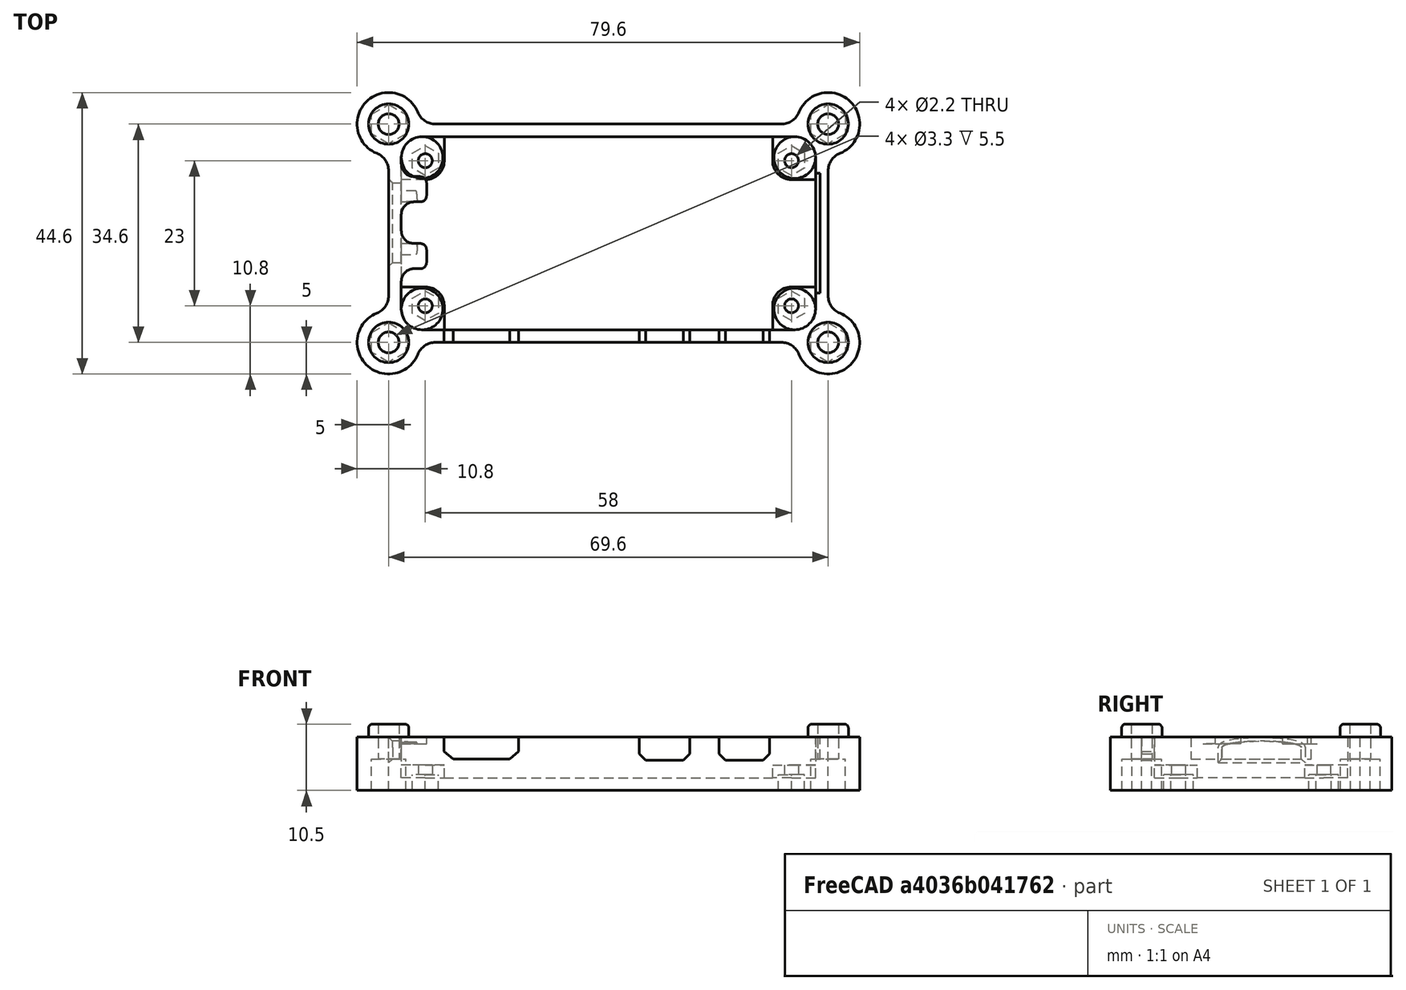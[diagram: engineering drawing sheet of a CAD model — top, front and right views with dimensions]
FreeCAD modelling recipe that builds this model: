
FCSTD DOCUMENT  (FreeCAD 0.18R13830 (Git))
Label: MMDVM_HS_Bottom-SLIM
License: CreativeCommons Attribution-NonCommercial-ShareAlike
LicenseURL: http://creativecommons.org/licenses/by-nc-sa/4.0/
objects: Sketcher::SketchObject×14, PartDesign::Pocket×7, PartDesign::Fillet×5, PartDesign::Pad×4, PartDesign::Hole×2, PartDesign::Chamfer×1, PartDesign::Body×1, Mesh::Feature×1
note: 47 computed .brp shape members not serialized (recipe doc carries the construction recipe); baked Part::Feature solids carry a one-line shape summary decoded from their .brp

FEATURE [Sketcher::SketchObject] Sketch
  MapMode = 5
  Support = -> [XY_Plane]
  sketch-geometry (24):
    g0: LineSegment [constr] StartX=-32.5 StartY=15 StartZ=0 EndX=32.5 EndY=15 EndZ=0
    g1: LineSegment [constr] StartX=32.5 StartY=15 StartZ=0 EndX=32.5 EndY=-15 EndZ=0
    g2: LineSegment [constr] StartX=32.5 StartY=-15 StartZ=0 EndX=-32.5 EndY=-15 EndZ=0
    g3: LineSegment [constr] StartX=-32.5 StartY=-15 StartZ=0 EndX=-32.5 EndY=15 EndZ=0
    g4: LineSegment [constr] StartX=-29 StartY=11.5 StartZ=0 EndX=29 EndY=11.5 EndZ=0
    g5: LineSegment [constr] StartX=29 StartY=11.5 StartZ=0 EndX=29 EndY=-11.5 EndZ=0
    g6: LineSegment [constr] StartX=29 StartY=-11.5 StartZ=0 EndX=-29 EndY=-11.5 EndZ=0
    g7: LineSegment [constr] StartX=-29 StartY=-11.5 StartZ=0 EndX=-29 EndY=11.5 EndZ=0
    g8: Circle CenterX=-29 CenterY=11.5 CenterZ=0 NormalX=0 NormalY=0 NormalZ=1 AngleXU=0 Radius=1.375
    g9: Circle CenterX=29 CenterY=11.5 CenterZ=0 NormalX=0 NormalY=0 NormalZ=1 AngleXU=0 Radius=1.375
    g10: Circle CenterX=29 CenterY=-11.5 CenterZ=0 NormalX=0 NormalY=0 NormalZ=1 AngleXU=0 Radius=1.375
    g11: Circle CenterX=-29 CenterY=-11.5 CenterZ=0 NormalX=0 NormalY=0 NormalZ=1 AngleXU=0 Radius=1.375
    g12: LineSegment [constr] StartX=-29.5 StartY=12 StartZ=0 EndX=29.5 EndY=12 EndZ=0
    g13: LineSegment [constr] StartX=29.5 StartY=12 StartZ=0 EndX=29.5 EndY=-12 EndZ=0
    g14: LineSegment [constr] StartX=29.5 StartY=-12 StartZ=0 EndX=-29.5 EndY=-12 EndZ=0
    g15: LineSegment [constr] StartX=-29.5 StartY=-12 StartZ=0 EndX=-29.5 EndY=12 EndZ=0
    g16: ArcOfCircle CenterX=-29.5 CenterY=12 CenterZ=0 NormalX=0 NormalY=0 NormalZ=1 AngleXU=0 Radius=3 StartAngle=1.5708 EndAngle=3.1416
    g17: ArcOfCircle CenterX=29.5 CenterY=12 CenterZ=0 NormalX=0 NormalY=0 NormalZ=1 AngleXU=0 Radius=3 StartAngle=1.42077e-07 EndAngle=1.5708
    g18: ArcOfCircle CenterX=29.5 CenterY=-12 CenterZ=0 NormalX=0 NormalY=0 NormalZ=1 AngleXU=0 Radius=3 StartAngle=4.71239 EndAngle=6.28319
    g19: ArcOfCircle CenterX=-29.5 CenterY=-12 CenterZ=0 NormalX=0 NormalY=0 NormalZ=1 AngleXU=0 Radius=3 StartAngle=3.14159 EndAngle=4.71239
    g20: LineSegment StartX=-29.5 StartY=15 StartZ=0 EndX=29.5 EndY=15 EndZ=0
    g21: LineSegment StartX=32.5 StartY=12 StartZ=0 EndX=32.5 EndY=-12 EndZ=0
    g22: LineSegment StartX=29.5 StartY=-15 StartZ=0 EndX=-29.5 EndY=-15 EndZ=0
    g23: LineSegment StartX=-32.5 StartY=-12 StartZ=0 EndX=-32.5 EndY=12 EndZ=0
  constraints (68):
    c: Coincident(g0,g1)
    c: Coincident(g1,g2)
    c: Coincident(g2,g3)
    c: Coincident(g3,g0)
    c: Horizontal(g0)
    c: Horizontal(g2)
    c: Vertical(g1)
    c: Vertical(g3)
    c: DistanceX(g0,g0) = 65
    c: DistanceY(g1,g1) = 30
    c: Symmetric(g0,g0,g-2)
    c: Symmetric(g0,g1,g-1)
    c: Coincident(g4,g5)
    c: Coincident(g5,g6)
    c: Coincident(g6,g7)
    c: Coincident(g7,g4)
    c: Horizontal(g4)
    c: Horizontal(g6)
    c: Vertical(g5)
    c: Vertical(g7)
    c: DistanceX(g4,g4) = 58
    c: DistanceY(g5,g5) = 23
    c: Symmetric(g4,g5,g-1)
    c: Symmetric(g4,g4,g-2)
    c: Coincident(g8,g4)
    c: Coincident(g9,g4)
    c: Coincident(g10,g5)
    c: Coincident(g11,g6)
    c: Radius(g11) = 1.375
    c: Radius(g8) = 1.375
    c: Radius(g9) = 1.375
    c: Radius(g10) = 1.375
    c: Coincident(g12,g13)
    c: Coincident(g13,g14)
    c: Coincident(g14,g15)
    c: Coincident(g15,g12)
    c: Horizontal(g12)
    c: Horizontal(g14)
    c: Vertical(g13)
    c: Vertical(g15)
    c: DistanceX(g4,g12) = 0.5
    c: DistanceY(g4,g12) = 0.5
    c: DistanceY(g13,g5) = 0.5
    c: DistanceX(g14,g6) = 0.5
    c: Coincident(g16,g12)
    c: Radius(g16) = 3
    c: Coincident(g17,g12)
    c: Radius(g17) = 3
    c: Coincident(g18,g13)
    c: Radius(g18) = 3
    c: Coincident(g19,g14)
    c: Radius(g19) = 3
    c: PointOnObject(g16,g0)
    c: PointOnObject(g17,g1)
    c: PointOnObject(g18,g2)
    c: PointOnObject(g19,g3)
    c: Coincident(g20,g16)
    c: Horizontal(g20)
    c: Coincident(g20,g17)
    c: Coincident(g21,g17)
    c: Vertical(g21)
    c: Coincident(g18,g21)
    c: Coincident(g22,g18)
    c: Horizontal(g22)
    c: Coincident(g19,g22)
    c: Coincident(g23,g19)
    c: Vertical(g23)
    c: Coincident(g23,g16)
FEATURE [Sketcher::SketchObject] Sketch001
  MapMode = 5
  Support = -> [XY_Plane]
  expr: Constraints[8] = Sketch.Constraints[8]
  expr: Constraints[41] = Sketch.Constraints[41]
  expr: Constraints[9] = Sketch.Constraints[9]
  expr: Constraints[45] = Sketch.Constraints[45]
  expr: Constraints[43] = Sketch.Constraints[43]
  expr: Constraints[42] = Sketch.Constraints[42]
  expr: Constraints[20] = Sketch.Constraints[20]
  expr: Constraints[21] = Sketch.Constraints[21]
  expr: Constraints[28] = Sketch.Constraints[28]
  expr: Constraints[29] = Sketch.Constraints[29]
  expr: Constraints[30] = Sketch.Constraints[30]
  expr: Constraints[40] = Sketch.Constraints[40]
  expr: Constraints[31] = Sketch.Constraints[31]
  expr: Constraints[47] = Sketch.Constraints[47]
  expr: Constraints[49] = Sketch.Constraints[49]
  expr: Constraints[51] = Sketch.Constraints[51]
  sketch-geometry (64):
    g0: LineSegment [constr] StartX=-32.5 StartY=15 StartZ=0 EndX=32.5 EndY=15 EndZ=0
    g1: LineSegment [constr] StartX=32.5 StartY=15 StartZ=0 EndX=32.5 EndY=-15 EndZ=0
    g2: LineSegment [constr] StartX=32.5 StartY=-15 StartZ=0 EndX=-32.5 EndY=-15 EndZ=0
    g3: LineSegment [constr] StartX=-32.5 StartY=-15 StartZ=0 EndX=-32.5 EndY=15 EndZ=0
    g4: LineSegment [constr] StartX=-29 StartY=11.5 StartZ=0 EndX=29 EndY=11.5 EndZ=0
    g5: LineSegment [constr] StartX=29 StartY=11.5 StartZ=0 EndX=29 EndY=-11.5 EndZ=0
    g6: LineSegment [constr] StartX=29 StartY=-11.5 StartZ=0 EndX=-29 EndY=-11.5 EndZ=0
    g7: LineSegment [constr] StartX=-29 StartY=-11.5 StartZ=0 EndX=-29 EndY=11.5 EndZ=0
    g8: Circle [constr] CenterX=-29 CenterY=11.5 CenterZ=0 NormalX=0 NormalY=0 NormalZ=1 AngleXU=0 Radius=1.375
    g9: Circle [constr] CenterX=29 CenterY=11.5 CenterZ=0 NormalX=0 NormalY=0 NormalZ=1 AngleXU=0 Radius=1.375
    g10: Circle [constr] CenterX=29 CenterY=-11.5 CenterZ=0 NormalX=0 NormalY=0 NormalZ=1 AngleXU=0 Radius=1.375
    g11: Circle [constr] CenterX=-29 CenterY=-11.5 CenterZ=0 NormalX=0 NormalY=0 NormalZ=1 AngleXU=0 Radius=1.375
    g12: LineSegment [constr] StartX=-29.5 StartY=12 StartZ=0 EndX=29.5 EndY=12 EndZ=0
    g13: LineSegment [constr] StartX=29.5 StartY=12 StartZ=0 EndX=29.5 EndY=-12 EndZ=0
    g14: LineSegment [constr] StartX=29.5 StartY=-12 StartZ=0 EndX=-29.5 EndY=-12 EndZ=0
    g15: LineSegment [constr] StartX=-29.5 StartY=-12 StartZ=0 EndX=-29.5 EndY=12 EndZ=0
    g16: ArcOfCircle [constr] CenterX=-29.5 CenterY=12 CenterZ=0 NormalX=0 NormalY=0 NormalZ=1 AngleXU=0 Radius=3 StartAngle=1.5708 EndAngle=3.14159
    g17: ArcOfCircle [constr] CenterX=29.5 CenterY=12 CenterZ=0 NormalX=0 NormalY=0 NormalZ=1 AngleXU=0 Radius=3 StartAngle=2.8425e-08 EndAngle=1.5708
    g18: ArcOfCircle [constr] CenterX=29.5 CenterY=-12 CenterZ=0 NormalX=0 NormalY=0 NormalZ=1 AngleXU=0 Radius=3 StartAngle=4.71239 EndAngle=6.28319
    g19: ArcOfCircle [constr] CenterX=-29.5 CenterY=-12 CenterZ=0 NormalX=0 NormalY=0 NormalZ=1 AngleXU=0 Radius=3 StartAngle=3.14159 EndAngle=4.71239
    g20: LineSegment [constr] StartX=-29.5 StartY=15 StartZ=0 EndX=29.5 EndY=15 EndZ=0
    g21: LineSegment [constr] StartX=32.5 StartY=12 StartZ=0 EndX=32.5 EndY=-12 EndZ=0
    g22: LineSegment [constr] StartX=29.5 StartY=-15 StartZ=0 EndX=-29.5 EndY=-15 EndZ=0
    g23: LineSegment [constr] StartX=-32.5 StartY=-12 StartZ=0 EndX=-32.5 EndY=12 EndZ=0
    g24: ArcOfCircle [constr] CenterX=-29.5 CenterY=12 CenterZ=0 NormalX=0 NormalY=0 NormalZ=1 AngleXU=0 Radius=3.3 StartAngle=1.5708 EndAngle=3.14159
    g25: ArcOfCircle [constr] CenterX=29.5 CenterY=12 CenterZ=0 NormalX=0 NormalY=0 NormalZ=1 AngleXU=0 Radius=3.3 StartAngle=-2.2e-10 EndAngle=1.5708
    g26: ArcOfCircle [constr] CenterX=29.5 CenterY=-12 CenterZ=0 NormalX=0 NormalY=0 NormalZ=1 AngleXU=0 Radius=3.3 StartAngle=4.71239 EndAngle=6.28319
    g27: ArcOfCircle [constr] CenterX=-29.5 CenterY=-12 CenterZ=0 NormalX=0 NormalY=0 NormalZ=1 AngleXU=0 Radius=3.3 StartAngle=3.14159 EndAngle=4.71239
    g28: LineSegment [constr] StartX=-32.8 StartY=12 StartZ=0 EndX=-32.8 EndY=-12 EndZ=0
    g29: LineSegment [constr] StartX=-29.5 StartY=15.3 StartZ=0 EndX=29.5 EndY=15.3 EndZ=0
    g30: LineSegment [constr] StartX=32.8 StartY=12 StartZ=0 EndX=32.8 EndY=-12 EndZ=0
    g31: LineSegment [constr] StartX=29.5 StartY=-15.3 StartZ=0 EndX=-29.5 EndY=-15.3 EndZ=0
    g32: LineSegment [constr] StartX=-34.8 StartY=17.3 StartZ=0 EndX=34.8 EndY=17.3 EndZ=0
    g33: LineSegment [constr] StartX=34.8 StartY=17.3 StartZ=0 EndX=34.8 EndY=-17.3 EndZ=0
    g34: LineSegment [constr] StartX=34.8 StartY=-17.3 StartZ=0 EndX=-34.8 EndY=-17.3 EndZ=0
    g35: LineSegment [constr] StartX=-34.8 StartY=-17.3 StartZ=0 EndX=-34.8 EndY=17.3 EndZ=0
    g36: Circle [constr] CenterX=34.8 CenterY=17.3 CenterZ=0 NormalX=0 NormalY=0 NormalZ=1 AngleXU=0 Radius=5
    g37: Circle [constr] CenterX=34.8 CenterY=-17.3 CenterZ=0 NormalX=0 NormalY=0 NormalZ=1 AngleXU=0 Radius=5
    g38: Circle [constr] CenterX=-34.8 CenterY=-17.3 CenterZ=0 NormalX=0 NormalY=0 NormalZ=1 AngleXU=0 Radius=5
    g39: Circle [constr] CenterX=-34.8 CenterY=17.3 CenterZ=0 NormalX=0 NormalY=0 NormalZ=1 AngleXU=0 Radius=5
    g40: Circle [constr] CenterX=27.3838 CenterY=20.3 CenterZ=0 NormalX=0 NormalY=0 NormalZ=1 AngleXU=0 Radius=3
    g41: Circle [constr] CenterX=-27.3838 CenterY=20.3 CenterZ=0 NormalX=0 NormalY=0 NormalZ=1 AngleXU=0 Radius=3
    g42: Circle [constr] CenterX=-37.8 CenterY=9.8838 CenterZ=0 NormalX=0 NormalY=0 NormalZ=1 AngleXU=0 Radius=3
    g43: Circle [constr] CenterX=-37.8 CenterY=-9.8838 CenterZ=0 NormalX=0 NormalY=0 NormalZ=1 AngleXU=0 Radius=3
    g44: Circle [constr] CenterX=-27.3838 CenterY=-20.3 CenterZ=0 NormalX=0 NormalY=0 NormalZ=1 AngleXU=0 Radius=3
    g45: Circle [constr] CenterX=27.3838 CenterY=-20.3 CenterZ=0 NormalX=0 NormalY=0 NormalZ=1 AngleXU=0 Radius=3
    g46: Circle [constr] CenterX=37.8 CenterY=-9.8838 CenterZ=0 NormalX=0 NormalY=0 NormalZ=1 AngleXU=0 Radius=3
    g47: Circle [constr] CenterX=37.8 CenterY=9.8838 CenterZ=0 NormalX=0 NormalY=0 NormalZ=1 AngleXU=0 Radius=3
    g48: ArcOfCircle CenterX=34.8 CenterY=17.3 CenterZ=0 NormalX=0 NormalY=0 NormalZ=1 AngleXU=0 Radius=5 StartAngle=5.09679 EndAngle=9.04038
    g49: ArcOfCircle CenterX=27.3838 CenterY=20.3 CenterZ=0 NormalX=0 NormalY=0 NormalZ=1 AngleXU=0 Radius=3 StartAngle=4.71239 EndAngle=5.89879
    g50: ArcOfCircle CenterX=37.8 CenterY=9.8838 CenterZ=0 NormalX=0 NormalY=0 NormalZ=1 AngleXU=0 Radius=3 StartAngle=1.95519 EndAngle=3.14159
    g51: ArcOfCircle CenterX=37.8 CenterY=-9.8838 CenterZ=0 NormalX=0 NormalY=0 NormalZ=1 AngleXU=0 Radius=3 StartAngle=3.14159 EndAngle=4.32799
    g52: ArcOfCircle CenterX=34.8 CenterY=-17.3 CenterZ=0 NormalX=0 NormalY=0 NormalZ=1 AngleXU=0 Radius=5 StartAngle=3.52599 EndAngle=7.46958
    g53: ArcOfCircle CenterX=27.3838 CenterY=-20.3 CenterZ=0 NormalX=0 NormalY=0 NormalZ=1 AngleXU=0 Radius=3 StartAngle=0.384397 EndAngle=1.5708
    g54: ArcOfCircle CenterX=-27.3838 CenterY=-20.3 CenterZ=0 NormalX=0 NormalY=0 NormalZ=1 AngleXU=0 Radius=3 StartAngle=1.5708 EndAngle=2.7572
    g55: ArcOfCircle CenterX=-34.8 CenterY=-17.3 CenterZ=0 NormalX=0 NormalY=0 NormalZ=1 AngleXU=0 Radius=5 StartAngle=1.95519 EndAngle=5.89879
    g56: ArcOfCircle CenterX=-37.8 CenterY=-9.8838 CenterZ=0 NormalX=0 NormalY=0 NormalZ=1 AngleXU=0 Radius=3 StartAngle=5.09679 EndAngle=6.28319
    g57: ArcOfCircle CenterX=-37.8 CenterY=9.8838 CenterZ=0 NormalX=0 NormalY=0 NormalZ=1 AngleXU=0 Radius=3 StartAngle=6.28319 EndAngle=7.46958
    g58: ArcOfCircle CenterX=-34.8 CenterY=17.3 CenterZ=0 NormalX=0 NormalY=0 NormalZ=1 AngleXU=0 Radius=5 StartAngle=0.384397 EndAngle=4.32799
    g59: ArcOfCircle CenterX=-27.3838 CenterY=20.3 CenterZ=0 NormalX=0 NormalY=0 NormalZ=1 AngleXU=0 Radius=3 StartAngle=3.52599 EndAngle=4.71239
    g60: LineSegment StartX=-27.3838 StartY=17.3 StartZ=0 EndX=27.3838 EndY=17.3 EndZ=0
    g61: LineSegment StartX=34.8 StartY=9.8838 StartZ=0 EndX=34.8 EndY=-9.8838 EndZ=0
    g62: LineSegment StartX=27.3838 StartY=-17.3 StartZ=0 EndX=-27.3838 EndY=-17.3 EndZ=0
    g63: LineSegment StartX=-34.8 StartY=-9.8838 StartZ=0 EndX=-34.8 EndY=9.8838 EndZ=0
  constraints (184):
    c: Coincident(g0,g1)
    c: Coincident(g1,g2)
    c: Coincident(g2,g3)
    c: Coincident(g3,g0)
    c: Horizontal(g0)
    c: Horizontal(g2)
    c: Vertical(g1)
    c: Vertical(g3)
    c: DistanceX(g0,g0) = 65
    c: DistanceY(g1,g1) = 30
    c: Symmetric(g0,g0,g-2)
    c: Symmetric(g0,g1,g-1)
    c: Coincident(g4,g5)
    c: Coincident(g5,g6)
    c: Coincident(g6,g7)
    c: Coincident(g7,g4)
    c: Horizontal(g4)
    c: Horizontal(g6)
    c: Vertical(g5)
    c: Vertical(g7)
    c: DistanceX(g4,g4) = 58
    c: DistanceY(g5,g5) = 23
    c: Symmetric(g4,g5,g-1)
    c: Symmetric(g4,g4,g-2)
    c: Coincident(g8,g4)
    c: Coincident(g9,g4)
    c: Coincident(g10,g5)
    c: Coincident(g11,g6)
    c: Radius(g11) = 1.375
    c: Radius(g8) = 1.375
    c: Radius(g9) = 1.375
    c: Radius(g10) = 1.375
    c: Coincident(g12,g13)
    c: Coincident(g13,g14)
    c: Coincident(g14,g15)
    c: Coincident(g15,g12)
    c: Horizontal(g12)
    c: Horizontal(g14)
    c: Vertical(g13)
    c: Vertical(g15)
    c: DistanceX(g4,g12) = 0.5
    c: DistanceY(g4,g12) = 0.5
    c: DistanceY(g13,g5) = 0.5
    c: DistanceX(g14,g6) = 0.5
    c: Coincident(g16,g12)
    c: Radius(g16) = 3
    c: Coincident(g17,g12)
    c: Radius(g17) = 3
    c: Coincident(g18,g13)
    c: Radius(g18) = 3
    c: Coincident(g19,g14)
    c: Radius(g19) = 3
    c: PointOnObject(g16,g0)
    c: PointOnObject(g17,g1)
    c: PointOnObject(g18,g2)
    c: PointOnObject(g19,g3)
    c: Coincident(g20,g16)
    c: Horizontal(g20)
    c: Coincident(g20,g17)
    c: Coincident(g21,g17)
    c: Vertical(g21)
    c: Coincident(g18,g21)
    c: Coincident(g22,g18)
    c: Horizontal(g22)
    c: Coincident(g19,g22)
    c: Coincident(g23,g19)
    c: Vertical(g23)
    c: Coincident(g23,g16)
    c: Coincident(g24,g12)
    c: Radius(g24) = 3.3
    c: Coincident(g25,g12)
    c: Radius(g25) = 3.3
    c: Coincident(g26,g13)
    c: Radius(g26) = 3.3
    c: Coincident(g27,g14)
    c: Radius(g27) = 3.3
    c: Vertical(g28)
    c: DistanceX(g28,g2) = 0.3
    c: Coincident(g27,g28)
    c: Coincident(g28,g24)
    c: Horizontal(g29)
    c: DistanceY(g0,g29) = 0.3
    c: Coincident(g24,g29)
    c: Coincident(g25,g29)
    c: Vertical(g30)
    c: DistanceX(g0,g30) = 0.3
    c: Coincident(g25,g30)
    c: Coincident(g30,g26)
    c: Horizontal(g31)
    c: DistanceY(g31,g1) = 0.3
    c: Coincident(g31,g26)
    c: Coincident(g31,g27)
    c: Coincident(g32,g33)
    c: Coincident(g33,g34)
    c: Coincident(g34,g35)
    c: Coincident(g35,g32)
    c: Horizontal(g32)
    c: Horizontal(g34)
    c: Vertical(g33)
    c: Vertical(g35)
    c: DistanceY(g25,g32) = 2
    c: DistanceX(g25,g32) = 2
    c: DistanceY(g33,g26) = 2
    c: DistanceX(g34,g27) = 2
    c: Coincident(g36,g32)
    c: Coincident(g37,g33)
    c: Coincident(g38,g34)
    c: Coincident(g39,g32)
    c: Radius(g39) = 5
    c: Radius(g38) = 5
    c: Radius(g37) = 5
    c: Radius(g36) = 5
    c: Radius(g40) = 3
    c: Tangent(g40,g36)
    c: Tangent(g40,g32)
    c: Tangent(g47,g36)
    c: Radius(g47) = 3
    c: Tangent(g47,g33)
    c: Radius(g46) = 3
    c: Tangent(g46,g37)
    c: Tangent(g46,g33)
    c: Radius(g45) = 3
    c: Tangent(g45,g37)
    c: Tangent(g45,g34)
    c: Radius(g44) = 3
    c: Tangent(g44,g34)
    c: Tangent(g44,g38)
    c: Radius(g43) = 3
    c: Tangent(g43,g38)
    c: Tangent(g43,g35)
    c: Radius(g42) = 3
    c: Tangent(g42,g35)
    c: Tangent(g42,g39)
    c: Radius(g41) = 3
    c: Tangent(g41,g32)
    c: Tangent(g41,g39)
    c: Coincident(g48,g32)
    c: PointOnObject(g48,g36)
    c: Coincident(g49,g40)
    c: PointOnObject(g49,g40)
    c: Coincident(g50,g47)
    c: PointOnObject(g50,g47)
    c: Coincident(g51,g46)
    c: PointOnObject(g51,g46)
    c: Coincident(g52,g33)
    c: PointOnObject(g52,g37)
    c: Coincident(g53,g45)
    c: PointOnObject(g53,g45)
    c: Coincident(g54,g44)
    c: PointOnObject(g54,g44)
    c: Coincident(g55,g34)
    c: PointOnObject(g55,g38)
    c: Coincident(g56,g43)
    c: PointOnObject(g56,g43)
    c: Coincident(g57,g42)
    c: PointOnObject(g57,g42)
    c: Coincident(g58,g32)
    c: PointOnObject(g58,g39)
    c: Coincident(g59,g41)
    c: PointOnObject(g59,g41)
    c: Coincident(g49,g48)
    c: Coincident(g48,g50)
    c: Coincident(g51,g52)
    c: Coincident(g52,g53)
    c: Coincident(g54,g55)
    c: Coincident(g55,g56)
    c: Coincident(g57,g58)
    c: Coincident(g58,g59)
    c: PointOnObject(g60,g32)
    c: Horizontal(g60)
    c: PointOnObject(g61,g33)
    c: Vertical(g61)
    c: PointOnObject(g62,g34)
    c: Horizontal(g62)
    c: PointOnObject(g63,g35)
    c: Vertical(g63)
    c: Coincident(g59,g60)
    c: Coincident(g60,g49)
    c: Coincident(g50,g61)
    c: Coincident(g61,g51)
    c: Coincident(g53,g62)
    c: Coincident(g54,g62)
    c: Coincident(g56,g63)
    c: Coincident(g57,g63)
FEATURE [PartDesign::Pad] Pad
  Length = 8.5
  Length2 = 100
  Profile = -> Sketch001
  Type = 0
FEATURE [Sketcher::SketchObject] Sketch002
  MapMode = 5
  Placement = pos=(0,0,8.5) rot=(0,0,1;0rad)
  Support = -> [Pad]
  expr: Constraints[133] = Sketch001.Constraints[133]
  expr: Constraints[130] = Sketch001.Constraints[130]
  expr: Constraints[112] = Sketch001.Constraints[112]
  expr: Constraints[127] = Sketch001.Constraints[127]
  expr: Constraints[124] = Sketch001.Constraints[124]
  expr: Constraints[110] = Sketch001.Constraints[110]
  expr: Constraints[51] = Sketch001.Constraints[51]
  expr: Constraints[100] = Sketch001.Constraints[100]
  expr: Constraints[77] = Sketch001.Constraints[77]
  expr: Constraints[89] = Sketch001.Constraints[89]
  expr: Constraints[118] = Sketch001.Constraints[118]
  expr: Constraints[85] = Sketch001.Constraints[85]
  expr: Constraints[103] = Sketch001.Constraints[103]
  expr: Constraints[111] = Sketch001.Constraints[111]
  expr: Constraints[71] = Sketch001.Constraints[71]
  expr: Constraints[49] = Sketch001.Constraints[49]
  expr: Constraints[102] = Sketch001.Constraints[102]
  expr: Constraints[69] = Sketch001.Constraints[69]
  expr: Constraints[47] = Sketch001.Constraints[47]
  expr: Constraints[73] = Sketch001.Constraints[73]
  expr: Constraints[75] = Sketch001.Constraints[75]
  expr: Constraints[31] = Sketch001.Constraints[31]
  expr: Constraints[116] = Sketch001.Constraints[116]
  expr: Constraints[40] = Sketch001.Constraints[40]
  expr: Constraints[30] = Sketch001.Constraints[30]
  expr: Constraints[29] = Sketch001.Constraints[29]
  expr: Constraints[121] = Sketch001.Constraints[121]
  expr: Constraints[28] = Sketch001.Constraints[28]
  expr: Constraints[21] = Sketch001.Constraints[21]
  expr: Constraints[20] = Sketch001.Constraints[20]
  expr: Constraints[45] = Sketch001.Constraints[45]
  expr: Constraints[108] = Sketch001.Constraints[108]
  expr: Constraints[43] = Sketch001.Constraints[43]
  expr: Constraints[42] = Sketch001.Constraints[42]
  expr: Constraints[101] = Sketch001.Constraints[101]
  expr: Constraints[109] = Sketch001.Constraints[109]
  expr: Constraints[41] = Sketch001.Constraints[41]
  expr: Constraints[9] = Sketch001.Constraints[9]
  expr: Constraints[81] = Sketch001.Constraints[81]
  expr: Constraints[8] = Sketch001.Constraints[8]
  sketch-geometry (64):
    g0: LineSegment [constr] StartX=-32.5 StartY=15 StartZ=0 EndX=32.5 EndY=15 EndZ=0
    g1: LineSegment [constr] StartX=32.5 StartY=15 StartZ=0 EndX=32.5 EndY=-15 EndZ=0
    g2: LineSegment [constr] StartX=32.5 StartY=-15 StartZ=0 EndX=-32.5 EndY=-15 EndZ=0
    g3: LineSegment [constr] StartX=-32.5 StartY=-15 StartZ=0 EndX=-32.5 EndY=15 EndZ=0
    g4: LineSegment [constr] StartX=-29 StartY=11.5 StartZ=0 EndX=29 EndY=11.5 EndZ=0
    g5: LineSegment [constr] StartX=29 StartY=11.5 StartZ=0 EndX=29 EndY=-11.5 EndZ=0
    g6: LineSegment [constr] StartX=29 StartY=-11.5 StartZ=0 EndX=-29 EndY=-11.5 EndZ=0
    g7: LineSegment [constr] StartX=-29 StartY=-11.5 StartZ=0 EndX=-29 EndY=11.5 EndZ=0
    g8: Circle [constr] CenterX=-29 CenterY=11.5 CenterZ=0 NormalX=0 NormalY=0 NormalZ=1 AngleXU=0 Radius=1.375
    g9: Circle [constr] CenterX=29 CenterY=11.5 CenterZ=0 NormalX=0 NormalY=0 NormalZ=1 AngleXU=0 Radius=1.375
    g10: Circle [constr] CenterX=29 CenterY=-11.5 CenterZ=0 NormalX=0 NormalY=0 NormalZ=1 AngleXU=0 Radius=1.375
    g11: Circle [constr] CenterX=-29 CenterY=-11.5 CenterZ=0 NormalX=0 NormalY=0 NormalZ=1 AngleXU=0 Radius=1.375
    g12: LineSegment [constr] StartX=-29.5 StartY=12 StartZ=0 EndX=29.5 EndY=12 EndZ=0
    g13: LineSegment [constr] StartX=29.5 StartY=12 StartZ=0 EndX=29.5 EndY=-12 EndZ=0
    g14: LineSegment [constr] StartX=29.5 StartY=-12 StartZ=0 EndX=-29.5 EndY=-12 EndZ=0
    g15: LineSegment [constr] StartX=-29.5 StartY=-12 StartZ=0 EndX=-29.5 EndY=12 EndZ=0
    g16: ArcOfCircle [constr] CenterX=-29.5 CenterY=12 CenterZ=0 NormalX=0 NormalY=0 NormalZ=1 AngleXU=0 Radius=3 StartAngle=1.5708 EndAngle=3.14159
    g17: ArcOfCircle [constr] CenterX=29.5 CenterY=12 CenterZ=0 NormalX=0 NormalY=0 NormalZ=1 AngleXU=0 Radius=3 StartAngle=2.8425e-08 EndAngle=1.5708
    g18: ArcOfCircle [constr] CenterX=29.5 CenterY=-12 CenterZ=0 NormalX=0 NormalY=0 NormalZ=1 AngleXU=0 Radius=3 StartAngle=4.71239 EndAngle=6.28319
    g19: ArcOfCircle [constr] CenterX=-29.5 CenterY=-12 CenterZ=0 NormalX=0 NormalY=0 NormalZ=1 AngleXU=0 Radius=3 StartAngle=3.14159 EndAngle=4.71239
    g20: LineSegment [constr] StartX=-29.5 StartY=15 StartZ=0 EndX=29.5 EndY=15 EndZ=0
    g21: LineSegment [constr] StartX=32.5 StartY=12 StartZ=0 EndX=32.5 EndY=-12 EndZ=0
    g22: LineSegment [constr] StartX=29.5 StartY=-15 StartZ=0 EndX=-29.5 EndY=-15 EndZ=0
    g23: LineSegment [constr] StartX=-32.5 StartY=-12 StartZ=0 EndX=-32.5 EndY=12 EndZ=0
    g24: ArcOfCircle CenterX=-29.5 CenterY=12 CenterZ=0 NormalX=0 NormalY=0 NormalZ=1 AngleXU=0 Radius=3.3 StartAngle=1.5708 EndAngle=3.14159
    g25: ArcOfCircle CenterX=29.5 CenterY=12 CenterZ=0 NormalX=0 NormalY=0 NormalZ=1 AngleXU=0 Radius=3.3 StartAngle=-2.2e-10 EndAngle=1.5708
    g26: ArcOfCircle CenterX=29.5 CenterY=-12 CenterZ=0 NormalX=0 NormalY=0 NormalZ=1 AngleXU=0 Radius=3.3 StartAngle=4.71239 EndAngle=6.28319
    g27: ArcOfCircle CenterX=-29.5 CenterY=-12 CenterZ=0 NormalX=0 NormalY=0 NormalZ=1 AngleXU=0 Radius=3.3 StartAngle=3.14159 EndAngle=4.71239
    g28: LineSegment StartX=-32.8 StartY=12 StartZ=0 EndX=-32.8 EndY=-12 EndZ=0
    g29: LineSegment StartX=-29.5 StartY=15.3 StartZ=0 EndX=29.5 EndY=15.3 EndZ=0
    g30: LineSegment StartX=32.8 StartY=12 StartZ=0 EndX=32.8 EndY=-12 EndZ=0
    g31: LineSegment StartX=29.5 StartY=-15.3 StartZ=0 EndX=-29.5 EndY=-15.3 EndZ=0
    g32: LineSegment [constr] StartX=-34.8 StartY=17.3 StartZ=0 EndX=34.8 EndY=17.3 EndZ=0
    g33: LineSegment [constr] StartX=34.8 StartY=17.3 StartZ=0 EndX=34.8 EndY=-17.3 EndZ=0
    g34: LineSegment [constr] StartX=34.8 StartY=-17.3 StartZ=0 EndX=-34.8 EndY=-17.3 EndZ=0
    g35: LineSegment [constr] StartX=-34.8 StartY=-17.3 StartZ=0 EndX=-34.8 EndY=17.3 EndZ=0
    g36: Circle [constr] CenterX=34.8 CenterY=17.3 CenterZ=0 NormalX=0 NormalY=0 NormalZ=1 AngleXU=0 Radius=5
    g37: Circle [constr] CenterX=34.8 CenterY=-17.3 CenterZ=0 NormalX=0 NormalY=0 NormalZ=1 AngleXU=0 Radius=5
    g38: Circle [constr] CenterX=-34.8 CenterY=-17.3 CenterZ=0 NormalX=0 NormalY=0 NormalZ=1 AngleXU=0 Radius=5
    g39: Circle [constr] CenterX=-34.8 CenterY=17.3 CenterZ=0 NormalX=0 NormalY=0 NormalZ=1 AngleXU=0 Radius=5
    g40: Circle [constr] CenterX=27.3838 CenterY=20.3 CenterZ=0 NormalX=0 NormalY=0 NormalZ=1 AngleXU=0 Radius=3
    g41: Circle [constr] CenterX=-27.3838 CenterY=20.3 CenterZ=0 NormalX=0 NormalY=0 NormalZ=1 AngleXU=0 Radius=3
    g42: Circle [constr] CenterX=-37.8 CenterY=9.8838 CenterZ=0 NormalX=0 NormalY=0 NormalZ=1 AngleXU=0 Radius=3
    g43: Circle [constr] CenterX=-37.8 CenterY=-9.8838 CenterZ=0 NormalX=0 NormalY=0 NormalZ=1 AngleXU=0 Radius=3
    g44: Circle [constr] CenterX=-27.3838 CenterY=-20.3 CenterZ=0 NormalX=0 NormalY=0 NormalZ=1 AngleXU=0 Radius=3
    g45: Circle [constr] CenterX=27.3838 CenterY=-20.3 CenterZ=0 NormalX=0 NormalY=0 NormalZ=1 AngleXU=0 Radius=3
    g46: Circle [constr] CenterX=37.8 CenterY=-9.8838 CenterZ=0 NormalX=0 NormalY=0 NormalZ=1 AngleXU=0 Radius=3
    g47: Circle [constr] CenterX=37.8 CenterY=9.8838 CenterZ=0 NormalX=0 NormalY=0 NormalZ=1 AngleXU=0 Radius=3
    g48: ArcOfCircle [constr] CenterX=34.8 CenterY=17.3 CenterZ=0 NormalX=0 NormalY=0 NormalZ=1 AngleXU=0 Radius=5 StartAngle=5.09679 EndAngle=9.04038
    g49: ArcOfCircle [constr] CenterX=27.3838 CenterY=20.3 CenterZ=0 NormalX=0 NormalY=0 NormalZ=1 AngleXU=0 Radius=3 StartAngle=4.71239 EndAngle=5.89879
    g50: ArcOfCircle [constr] CenterX=37.8 CenterY=9.8838 CenterZ=0 NormalX=0 NormalY=0 NormalZ=1 AngleXU=0 Radius=3 StartAngle=1.95519 EndAngle=3.14159
    g51: ArcOfCircle [constr] CenterX=37.8 CenterY=-9.8838 CenterZ=0 NormalX=0 NormalY=0 NormalZ=1 AngleXU=0 Radius=3 StartAngle=3.14159 EndAngle=4.32799
    g52: ArcOfCircle [constr] CenterX=34.8 CenterY=-17.3 CenterZ=0 NormalX=0 NormalY=0 NormalZ=1 AngleXU=0 Radius=5 StartAngle=3.52599 EndAngle=7.46958
    g53: ArcOfCircle [constr] CenterX=27.3838 CenterY=-20.3 CenterZ=0 NormalX=0 NormalY=0 NormalZ=1 AngleXU=0 Radius=3 StartAngle=0.384397 EndAngle=1.5708
    g54: ArcOfCircle [constr] CenterX=-27.3838 CenterY=-20.3 CenterZ=0 NormalX=0 NormalY=0 NormalZ=1 AngleXU=0 Radius=3 StartAngle=1.5708 EndAngle=2.7572
    g55: ArcOfCircle [constr] CenterX=-34.8 CenterY=-17.3 CenterZ=0 NormalX=0 NormalY=0 NormalZ=1 AngleXU=0 Radius=5 StartAngle=1.95519 EndAngle=5.89879
    g56: ArcOfCircle [constr] CenterX=-37.8 CenterY=-9.8838 CenterZ=0 NormalX=0 NormalY=0 NormalZ=1 AngleXU=0 Radius=3 StartAngle=5.09679 EndAngle=6.28319
    g57: ArcOfCircle [constr] CenterX=-37.8 CenterY=9.8838 CenterZ=0 NormalX=0 NormalY=0 NormalZ=1 AngleXU=0 Radius=3 StartAngle=6.28319 EndAngle=7.46958
    g58: ArcOfCircle [constr] CenterX=-34.8 CenterY=17.3 CenterZ=0 NormalX=0 NormalY=0 NormalZ=1 AngleXU=0 Radius=5 StartAngle=0.384397 EndAngle=4.32799
    g59: ArcOfCircle [constr] CenterX=-27.3838 CenterY=20.3 CenterZ=0 NormalX=0 NormalY=0 NormalZ=1 AngleXU=0 Radius=3 StartAngle=3.52599 EndAngle=4.71239
    g60: LineSegment [constr] StartX=-27.3838 StartY=17.3 StartZ=0 EndX=27.3838 EndY=17.3 EndZ=0
    g61: LineSegment [constr] StartX=34.8 StartY=9.8838 StartZ=0 EndX=34.8 EndY=-9.8838 EndZ=0
    g62: LineSegment [constr] StartX=27.3838 StartY=-17.3 StartZ=0 EndX=-27.3838 EndY=-17.3 EndZ=0
    g63: LineSegment [constr] StartX=-34.8 StartY=-9.8838 StartZ=0 EndX=-34.8 EndY=9.8838 EndZ=0
  constraints (184):
    c: Coincident(g0,g1)
    c: Coincident(g1,g2)
    c: Coincident(g2,g3)
    c: Coincident(g3,g0)
    c: Horizontal(g0)
    c: Horizontal(g2)
    c: Vertical(g1)
    c: Vertical(g3)
    c: DistanceX(g0,g0) = 65
    c: DistanceY(g1,g1) = 30
    c: Symmetric(g0,g0,g-2)
    c: Symmetric(g0,g1,g-1)
    c: Coincident(g4,g5)
    c: Coincident(g5,g6)
    c: Coincident(g6,g7)
    c: Coincident(g7,g4)
    c: Horizontal(g4)
    c: Horizontal(g6)
    c: Vertical(g5)
    c: Vertical(g7)
    c: DistanceX(g4,g4) = 58
    c: DistanceY(g5,g5) = 23
    c: Symmetric(g4,g5,g-1)
    c: Symmetric(g4,g4,g-2)
    c: Coincident(g8,g4)
    c: Coincident(g9,g4)
    c: Coincident(g10,g5)
    c: Coincident(g11,g6)
    c: Radius(g11) = 1.375
    c: Radius(g8) = 1.375
    c: Radius(g9) = 1.375
    c: Radius(g10) = 1.375
    c: Coincident(g12,g13)
    c: Coincident(g13,g14)
    c: Coincident(g14,g15)
    c: Coincident(g15,g12)
    c: Horizontal(g12)
    c: Horizontal(g14)
    c: Vertical(g13)
    c: Vertical(g15)
    c: DistanceX(g4,g12) = 0.5
    c: DistanceY(g4,g12) = 0.5
    c: DistanceY(g13,g5) = 0.5
    c: DistanceX(g14,g6) = 0.5
    c: Coincident(g16,g12)
    c: Radius(g16) = 3
    c: Coincident(g17,g12)
    c: Radius(g17) = 3
    c: Coincident(g18,g13)
    c: Radius(g18) = 3
    c: Coincident(g19,g14)
    c: Radius(g19) = 3
    c: PointOnObject(g16,g0)
    c: PointOnObject(g17,g1)
    c: PointOnObject(g18,g2)
    c: PointOnObject(g19,g3)
    c: Coincident(g20,g16)
    c: Horizontal(g20)
    c: Coincident(g20,g17)
    c: Coincident(g21,g17)
    c: Vertical(g21)
    c: Coincident(g18,g21)
    c: Coincident(g22,g18)
    c: Horizontal(g22)
    c: Coincident(g19,g22)
    c: Coincident(g23,g19)
    c: Vertical(g23)
    c: Coincident(g23,g16)
    c: Coincident(g24,g12)
    c: Radius(g24) = 3.3
    c: Coincident(g25,g12)
    c: Radius(g25) = 3.3
    c: Coincident(g26,g13)
    c: Radius(g26) = 3.3
    c: Coincident(g27,g14)
    c: Radius(g27) = 3.3
    c: Vertical(g28)
    c: DistanceX(g28,g2) = 0.3
    c: Coincident(g27,g28)
    c: Coincident(g28,g24)
    c: Horizontal(g29)
    c: DistanceY(g0,g29) = 0.3
    c: Coincident(g24,g29)
    c: Coincident(g25,g29)
    c: Vertical(g30)
    c: DistanceX(g0,g30) = 0.3
    c: Coincident(g25,g30)
    c: Coincident(g30,g26)
    c: Horizontal(g31)
    c: DistanceY(g31,g1) = 0.3
    c: Coincident(g31,g26)
    c: Coincident(g31,g27)
    c: Coincident(g32,g33)
    c: Coincident(g33,g34)
    c: Coincident(g34,g35)
    c: Coincident(g35,g32)
    c: Horizontal(g32)
    c: Horizontal(g34)
    c: Vertical(g33)
    c: Vertical(g35)
    c: DistanceY(g25,g32) = 2
    c: DistanceX(g25,g32) = 2
    c: DistanceY(g33,g26) = 2
    c: DistanceX(g34,g27) = 2
    c: Coincident(g36,g32)
    c: Coincident(g37,g33)
    c: Coincident(g38,g34)
    c: Coincident(g39,g32)
    c: Radius(g39) = 5
    c: Radius(g38) = 5
    c: Radius(g37) = 5
    c: Radius(g36) = 5
    c: Radius(g40) = 3
    c: Tangent(g40,g36)
    c: Tangent(g40,g32)
    c: Tangent(g47,g36)
    c: Radius(g47) = 3
    c: Tangent(g47,g33)
    c: Radius(g46) = 3
    c: Tangent(g46,g37)
    c: Tangent(g46,g33)
    c: Radius(g45) = 3
    c: Tangent(g45,g37)
    c: Tangent(g45,g34)
    c: Radius(g44) = 3
    c: Tangent(g44,g34)
    c: Tangent(g44,g38)
    c: Radius(g43) = 3
    c: Tangent(g43,g38)
    c: Tangent(g43,g35)
    c: Radius(g42) = 3
    c: Tangent(g42,g35)
    c: Tangent(g42,g39)
    c: Radius(g41) = 3
    c: Tangent(g41,g32)
    c: Tangent(g41,g39)
    c: Coincident(g48,g32)
    c: PointOnObject(g48,g36)
    c: Coincident(g49,g40)
    c: PointOnObject(g49,g40)
    c: Coincident(g50,g47)
    c: PointOnObject(g50,g47)
    c: Coincident(g51,g46)
    c: PointOnObject(g51,g46)
    c: Coincident(g52,g33)
    c: PointOnObject(g52,g37)
    c: Coincident(g53,g45)
    c: PointOnObject(g53,g45)
    c: Coincident(g54,g44)
    c: PointOnObject(g54,g44)
    c: Coincident(g55,g34)
    c: PointOnObject(g55,g38)
    c: Coincident(g56,g43)
    c: PointOnObject(g56,g43)
    c: Coincident(g57,g42)
    c: PointOnObject(g57,g42)
    c: Coincident(g58,g32)
    c: PointOnObject(g58,g39)
    c: Coincident(g59,g41)
    c: PointOnObject(g59,g41)
    c: Coincident(g49,g48)
    c: Coincident(g48,g50)
    c: Coincident(g51,g52)
    c: Coincident(g52,g53)
    c: Coincident(g54,g55)
    c: Coincident(g55,g56)
    c: Coincident(g57,g58)
    c: Coincident(g58,g59)
    c: PointOnObject(g60,g32)
    c: Horizontal(g60)
    c: PointOnObject(g61,g33)
    c: Vertical(g61)
    c: PointOnObject(g62,g34)
    c: Horizontal(g62)
    c: PointOnObject(g63,g35)
    c: Vertical(g63)
    c: Coincident(g59,g60)
    c: Coincident(g60,g49)
    c: Coincident(g50,g61)
    c: Coincident(g61,g51)
    c: Coincident(g53,g62)
    c: Coincident(g54,g62)
    c: Coincident(g56,g63)
    c: Coincident(g57,g63)
FEATURE [PartDesign::Pocket] Pocket
  BaseFeature = -> Pad
  Length = 6.5
  Length2 = 100
  Profile = -> Sketch002
  Type = 0
FEATURE [Sketcher::SketchObject] Sketch003
  MapMode = 5
  Placement = pos=(0,0,2) rot=(0,0,1;0rad)
  Support = -> [Pocket]
  expr: Constraints[133] = Sketch002.Constraints[133]
  expr: Constraints[130] = Sketch002.Constraints[130]
  expr: Constraints[112] = Sketch002.Constraints[112]
  expr: Constraints[124] = Sketch002.Constraints[124]
  expr: Constraints[127] = Sketch002.Constraints[127]
  expr: Constraints[110] = Sketch002.Constraints[110]
  expr: Constraints[51] = Sketch002.Constraints[51]
  expr: Constraints[100] = Sketch002.Constraints[100]
  expr: Constraints[77] = Sketch002.Constraints[77]
  expr: Constraints[89] = Sketch002.Constraints[89]
  expr: Constraints[118] = Sketch002.Constraints[118]
  expr: Constraints[85] = Sketch002.Constraints[85]
  expr: Constraints[71] = Sketch002.Constraints[71]
  expr: Constraints[103] = Sketch002.Constraints[103]
  expr: Constraints[111] = Sketch002.Constraints[111]
  expr: Constraints[102] = Sketch002.Constraints[102]
  expr: Constraints[49] = Sketch002.Constraints[49]
  expr: Constraints[69] = Sketch002.Constraints[69]
  expr: Constraints[75] = Sketch002.Constraints[75]
  expr: Constraints[73] = Sketch002.Constraints[73]
  expr: Constraints[47] = Sketch002.Constraints[47]
  expr: Constraints[31] = Sketch002.Constraints[31]
  expr: Constraints[40] = Sketch002.Constraints[40]
  expr: Constraints[116] = Sketch002.Constraints[116]
  expr: Constraints[30] = Sketch002.Constraints[30]
  expr: Constraints[29] = Sketch002.Constraints[29]
  expr: Constraints[28] = Sketch002.Constraints[28]
  expr: Constraints[121] = Sketch002.Constraints[121]
  expr: Constraints[21] = Sketch002.Constraints[21]
  expr: Constraints[20] = Sketch002.Constraints[20]
  expr: Constraints[108] = Sketch002.Constraints[108]
  expr: Constraints[45] = Sketch002.Constraints[45]
  expr: Constraints[43] = Sketch002.Constraints[43]
  expr: Constraints[42] = Sketch002.Constraints[42]
  expr: Constraints[101] = Sketch002.Constraints[101]
  expr: Constraints[109] = Sketch002.Constraints[109]
  expr: Constraints[41] = Sketch002.Constraints[41]
  expr: Constraints[9] = Sketch002.Constraints[9]
  expr: Constraints[81] = Sketch002.Constraints[81]
  expr: Constraints[8] = Sketch002.Constraints[8]
  sketch-geometry (92):
    g0: LineSegment [constr] StartX=-32.5 StartY=15 StartZ=0 EndX=32.5 EndY=15 EndZ=0
    g1: LineSegment [constr] StartX=32.5 StartY=15 StartZ=0 EndX=32.5 EndY=-15 EndZ=0
    g2: LineSegment [constr] StartX=32.5 StartY=-15 StartZ=0 EndX=-32.5 EndY=-15 EndZ=0
    g3: LineSegment [constr] StartX=-32.5 StartY=-15 StartZ=0 EndX=-32.5 EndY=15 EndZ=0
    g4: LineSegment [constr] StartX=-29 StartY=11.5 StartZ=0 EndX=29 EndY=11.5 EndZ=0
    g5: LineSegment [constr] StartX=29 StartY=11.5 StartZ=0 EndX=29 EndY=-11.5 EndZ=0
    g6: LineSegment [constr] StartX=29 StartY=-11.5 StartZ=0 EndX=-29 EndY=-11.5 EndZ=0
    g7: LineSegment [constr] StartX=-29 StartY=-11.5 StartZ=0 EndX=-29 EndY=11.5 EndZ=0
    g8: Circle [constr] CenterX=-29 CenterY=11.5 CenterZ=0 NormalX=0 NormalY=0 NormalZ=1 AngleXU=0 Radius=1.375
    g9: Circle [constr] CenterX=29 CenterY=11.5 CenterZ=0 NormalX=0 NormalY=0 NormalZ=1 AngleXU=0 Radius=1.375
    g10: Circle [constr] CenterX=29 CenterY=-11.5 CenterZ=0 NormalX=0 NormalY=0 NormalZ=1 AngleXU=0 Radius=1.375
    g11: Circle [constr] CenterX=-29 CenterY=-11.5 CenterZ=0 NormalX=0 NormalY=0 NormalZ=1 AngleXU=0 Radius=1.375
    g12: LineSegment [constr] StartX=-29.5 StartY=12 StartZ=0 EndX=29.5 EndY=12 EndZ=0
    g13: LineSegment [constr] StartX=29.5 StartY=12 StartZ=0 EndX=29.5 EndY=-12 EndZ=0
    g14: LineSegment [constr] StartX=29.5 StartY=-12 StartZ=0 EndX=-29.5 EndY=-12 EndZ=0
    g15: LineSegment [constr] StartX=-29.5 StartY=-12 StartZ=0 EndX=-29.5 EndY=12 EndZ=0
    g16: ArcOfCircle [constr] CenterX=-29.5 CenterY=12 CenterZ=0 NormalX=0 NormalY=0 NormalZ=1 AngleXU=0 Radius=3 StartAngle=1.5708 EndAngle=3.14159
    g17: ArcOfCircle [constr] CenterX=29.5 CenterY=12 CenterZ=0 NormalX=0 NormalY=0 NormalZ=1 AngleXU=0 Radius=3 StartAngle=3.6972e-08 EndAngle=1.5708
    g18: ArcOfCircle [constr] CenterX=29.5 CenterY=-12 CenterZ=0 NormalX=0 NormalY=0 NormalZ=1 AngleXU=0 Radius=3 StartAngle=4.71239 EndAngle=6.28319
    g19: ArcOfCircle [constr] CenterX=-29.5 CenterY=-12 CenterZ=0 NormalX=0 NormalY=0 NormalZ=1 AngleXU=0 Radius=3 StartAngle=3.14159 EndAngle=4.71239
    g20: LineSegment [constr] StartX=-29.5 StartY=15 StartZ=0 EndX=29.5 EndY=15 EndZ=0
    g21: LineSegment [constr] StartX=32.5 StartY=12 StartZ=0 EndX=32.5 EndY=-12 EndZ=0
    g22: LineSegment [constr] StartX=29.5 StartY=-15 StartZ=0 EndX=-29.5 EndY=-15 EndZ=0
    g23: LineSegment [constr] StartX=-32.5 StartY=-12 StartZ=0 EndX=-32.5 EndY=12 EndZ=0
    g24: ArcOfCircle [constr] CenterX=-29.5 CenterY=12 CenterZ=0 NormalX=0 NormalY=0 NormalZ=1 AngleXU=0 Radius=3.3 StartAngle=1.5708 EndAngle=3.14159
    g25: ArcOfCircle [constr] CenterX=29.5 CenterY=12 CenterZ=0 NormalX=0 NormalY=0 NormalZ=1 AngleXU=0 Radius=3.3 StartAngle=-4.27e-10 EndAngle=1.5708
    g26: ArcOfCircle [constr] CenterX=29.5 CenterY=-12 CenterZ=0 NormalX=0 NormalY=0 NormalZ=1 AngleXU=0 Radius=3.3 StartAngle=4.71239 EndAngle=6.28319
    g27: ArcOfCircle [constr] CenterX=-29.5 CenterY=-12 CenterZ=0 NormalX=0 NormalY=0 NormalZ=1 AngleXU=0 Radius=3.3 StartAngle=3.14159 EndAngle=4.71239
    g28: LineSegment [constr] StartX=-32.8 StartY=12 StartZ=0 EndX=-32.8 EndY=-12 EndZ=0
    g29: LineSegment [constr] StartX=-29.5 StartY=15.3 StartZ=0 EndX=29.5 EndY=15.3 EndZ=0
    g30: LineSegment [constr] StartX=32.8 StartY=12 StartZ=0 EndX=32.8 EndY=-12 EndZ=0
    g31: LineSegment [constr] StartX=29.5 StartY=-15.3 StartZ=0 EndX=-29.5 EndY=-15.3 EndZ=0
    g32: LineSegment [constr] StartX=-34.8 StartY=17.3 StartZ=0 EndX=34.8 EndY=17.3 EndZ=0
    g33: LineSegment [constr] StartX=34.8 StartY=17.3 StartZ=0 EndX=34.8 EndY=-17.3 EndZ=0
    g34: LineSegment [constr] StartX=34.8 StartY=-17.3 StartZ=0 EndX=-34.8 EndY=-17.3 EndZ=0
    g35: LineSegment [constr] StartX=-34.8 StartY=-17.3 StartZ=0 EndX=-34.8 EndY=17.3 EndZ=0
    g36: Circle [constr] CenterX=34.8 CenterY=17.3 CenterZ=0 NormalX=0 NormalY=0 NormalZ=1 AngleXU=0 Radius=5
    g37: Circle [constr] CenterX=34.8 CenterY=-17.3 CenterZ=0 NormalX=0 NormalY=0 NormalZ=1 AngleXU=0 Radius=5
    g38: Circle [constr] CenterX=-34.8 CenterY=-17.3 CenterZ=0 NormalX=0 NormalY=0 NormalZ=1 AngleXU=0 Radius=5
    g39: Circle [constr] CenterX=-34.8 CenterY=17.3 CenterZ=0 NormalX=0 NormalY=0 NormalZ=1 AngleXU=0 Radius=5
    g40: Circle [constr] CenterX=27.3838 CenterY=20.3 CenterZ=0 NormalX=0 NormalY=0 NormalZ=1 AngleXU=0 Radius=3
    g41: Circle [constr] CenterX=-27.3838 CenterY=20.3 CenterZ=0 NormalX=0 NormalY=0 NormalZ=1 AngleXU=0 Radius=3
    g42: Circle [constr] CenterX=-37.8 CenterY=9.8838 CenterZ=0 NormalX=0 NormalY=0 NormalZ=1 AngleXU=0 Radius=3
    g43: Circle [constr] CenterX=-37.8 CenterY=-9.8838 CenterZ=0 NormalX=0 NormalY=0 NormalZ=1 AngleXU=0 Radius=3
    g44: Circle [constr] CenterX=-27.3838 CenterY=-20.3 CenterZ=0 NormalX=0 NormalY=0 NormalZ=1 AngleXU=0 Radius=3
    g45: Circle [constr] CenterX=27.3838 CenterY=-20.3 CenterZ=0 NormalX=0 NormalY=0 NormalZ=1 AngleXU=0 Radius=3
    g46: Circle [constr] CenterX=37.8 CenterY=-9.8838 CenterZ=0 NormalX=0 NormalY=0 NormalZ=1 AngleXU=0 Radius=3
    g47: Circle [constr] CenterX=37.8 CenterY=9.8838 CenterZ=0 NormalX=0 NormalY=0 NormalZ=1 AngleXU=0 Radius=3
    g48: ArcOfCircle [constr] CenterX=34.8 CenterY=17.3 CenterZ=0 NormalX=0 NormalY=0 NormalZ=1 AngleXU=0 Radius=5 StartAngle=5.09679 EndAngle=9.04038
    g49: ArcOfCircle [constr] CenterX=27.3838 CenterY=20.3 CenterZ=0 NormalX=0 NormalY=0 NormalZ=1 AngleXU=0 Radius=3 StartAngle=4.71239 EndAngle=5.89879
    g50: ArcOfCircle [constr] CenterX=37.8 CenterY=9.8838 CenterZ=0 NormalX=0 NormalY=0 NormalZ=1 AngleXU=0 Radius=3 StartAngle=1.95519 EndAngle=3.14159
    g51: ArcOfCircle [constr] CenterX=37.8 CenterY=-9.8838 CenterZ=0 NormalX=0 NormalY=0 NormalZ=1 AngleXU=0 Radius=3 StartAngle=3.14159 EndAngle=4.32799
    g52: ArcOfCircle [constr] CenterX=34.8 CenterY=-17.3 CenterZ=0 NormalX=0 NormalY=0 NormalZ=1 AngleXU=0 Radius=5 StartAngle=3.52599 EndAngle=7.46958
    g53: ArcOfCircle [constr] CenterX=27.3838 CenterY=-20.3 CenterZ=0 NormalX=0 NormalY=0 NormalZ=1 AngleXU=0 Radius=3 StartAngle=0.384397 EndAngle=1.5708
    g54: ArcOfCircle [constr] CenterX=-27.3838 CenterY=-20.3 CenterZ=0 NormalX=0 NormalY=0 NormalZ=1 AngleXU=0 Radius=3 StartAngle=1.5708 EndAngle=2.7572
    g55: ArcOfCircle [constr] CenterX=-34.8 CenterY=-17.3 CenterZ=0 NormalX=0 NormalY=0 NormalZ=1 AngleXU=0 Radius=5 StartAngle=1.95519 EndAngle=5.89879
    g56: ArcOfCircle [constr] CenterX=-37.8 CenterY=-9.8838 CenterZ=0 NormalX=0 NormalY=0 NormalZ=1 AngleXU=0 Radius=3 StartAngle=5.09678 EndAngle=6.28319
    g57: ArcOfCircle [constr] CenterX=-37.8 CenterY=9.8838 CenterZ=0 NormalX=0 NormalY=0 NormalZ=1 AngleXU=0 Radius=3 StartAngle=4.4909e-08 EndAngle=1.1864
    g58: ArcOfCircle [constr] CenterX=-34.8 CenterY=17.3 CenterZ=0 NormalX=0 NormalY=0 NormalZ=1 AngleXU=0 Radius=5 StartAngle=0.384397 EndAngle=4.32799
    g59: ArcOfCircle [constr] CenterX=-27.3838 CenterY=20.3 CenterZ=0 NormalX=0 NormalY=0 NormalZ=1 AngleXU=0 Radius=3 StartAngle=3.52599 EndAngle=4.71239
    g60: LineSegment [constr] StartX=-27.3838 StartY=17.3 StartZ=0 EndX=27.3838 EndY=17.3 EndZ=0
    g61: LineSegment [constr] StartX=34.8 StartY=9.8838 StartZ=0 EndX=34.8 EndY=-9.8838 EndZ=0
    g62: LineSegment [constr] StartX=27.3838 StartY=-17.3 StartZ=0 EndX=-27.3838 EndY=-17.3 EndZ=0
    g63: LineSegment [constr] StartX=-34.8 StartY=-9.8838 StartZ=0 EndX=-34.8 EndY=9.8838 EndZ=0
    g64: ArcOfCircle CenterX=29 CenterY=11.5 CenterZ=0 NormalX=0 NormalY=0 NormalZ=1 AngleXU=0 Radius=3 StartAngle=3.14352 EndAngle=4.71046
    g65: ArcOfCircle CenterX=29.5 CenterY=12 CenterZ=0 NormalX=0 NormalY=0 NormalZ=1 AngleXU=0 Radius=3.3 StartAngle=2.17631e-07 EndAngle=1.5708
    g66: LineSegment StartX=26 StartY=15.3 StartZ=0 EndX=29.5 EndY=15.3 EndZ=0
    g67: LineSegment StartX=32.8 StartY=12 StartZ=0 EndX=32.8 EndY=8.50001 EndZ=0
    g68: LineSegment StartX=26 StartY=15.3 StartZ=0 EndX=26 EndY=11.4942 EndZ=0
    g69: LineSegment StartX=28.9942 StartY=8.50001 StartZ=0 EndX=32.8 EndY=8.50001 EndZ=0
    g70: LineSegment [constr] StartX=-43.6068 StartY=0 StartZ=0 EndX=51.9839 EndY=0 EndZ=0
    g71: LineSegment [constr] StartX=0 StartY=-19.8111 StartZ=0 EndX=0 EndY=22.459 EndZ=0
    g72: LineSegment StartX=26 StartY=-15.3 StartZ=0 EndX=26 EndY=-11.4942 EndZ=0
    g73: ArcOfCircle CenterX=29 CenterY=-11.5 CenterZ=0 NormalX=0 NormalY=0 NormalZ=1 AngleXU=0 Radius=3 StartAngle=1.57273 EndAngle=3.13966
    g74: LineSegment StartX=28.9942 StartY=-8.50001 StartZ=0 EndX=32.8 EndY=-8.50001 EndZ=0
    g75: LineSegment StartX=26 StartY=-15.3 StartZ=0 EndX=29.5 EndY=-15.3 EndZ=0
    g76: ArcOfCircle CenterX=29.5 CenterY=-12 CenterZ=0 NormalX=0 NormalY=0 NormalZ=1 AngleXU=0 Radius=3.3 StartAngle=4.71238 EndAngle=6.28319
    g77: LineSegment StartX=32.8 StartY=-12 StartZ=0 EndX=32.8 EndY=-8.50001 EndZ=0
    g78: LineSegment StartX=-28.9942 StartY=-8.50001 StartZ=0 EndX=-32.8 EndY=-8.50001 EndZ=0
    g79: LineSegment StartX=-32.8 StartY=-12 StartZ=0 EndX=-32.8 EndY=-8.50001 EndZ=0
    g80: ArcOfCircle CenterX=-29.5 CenterY=-12 CenterZ=0 NormalX=0 NormalY=0 NormalZ=1 AngleXU=0 Radius=3.3 StartAngle=3.14159 EndAngle=4.71239
    g81: LineSegment StartX=-26 StartY=-15.3 StartZ=0 EndX=-29.5 EndY=-15.3 EndZ=0
    g82: LineSegment StartX=-26 StartY=-15.3 StartZ=0 EndX=-26 EndY=-11.4942 EndZ=0
    g83: ArcOfCircle CenterX=-29 CenterY=-11.5 CenterZ=0 NormalX=0 NormalY=0 NormalZ=1 AngleXU=0 Radius=3 StartAngle=0.00192871 EndAngle=1.56886
    g84: LineSegment StartX=-28.9942 StartY=8.50001 StartZ=0 EndX=-32.8 EndY=8.50001 EndZ=0
    g85: LineSegment StartX=-32.8 StartY=12 StartZ=0 EndX=-32.8 EndY=8.50001 EndZ=0
    g86: ArcOfCircle CenterX=-29.5 CenterY=12 CenterZ=0 NormalX=0 NormalY=0 NormalZ=1 AngleXU=0 Radius=3.3 StartAngle=1.57079 EndAngle=3.14159
    g87: LineSegment StartX=-26 StartY=15.3 StartZ=0 EndX=-29.5 EndY=15.3 EndZ=0
    g88: LineSegment StartX=-26 StartY=15.3 StartZ=0 EndX=-26 EndY=11.4942 EndZ=0
    g89: ArcOfCircle CenterX=-29 CenterY=11.5 CenterZ=0 NormalX=0 NormalY=0 NormalZ=1 AngleXU=0 Radius=3 StartAngle=4.71432 EndAngle=6.28126
    g90: Circle CenterX=29 CenterY=11.5 CenterZ=0 NormalX=0 NormalY=0 NormalZ=1 AngleXU=0 Radius=0.5
    g91: Circle CenterX=-29 CenterY=-11.5 CenterZ=0 NormalX=0 NormalY=0 NormalZ=1 AngleXU=0 Radius=0.5
  constraints (241):
    c: Coincident(g0,g1)
    c: Coincident(g1,g2)
    c: Coincident(g2,g3)
    c: Coincident(g3,g0)
    c: Horizontal(g0)
    c: Horizontal(g2)
    c: Vertical(g1)
    c: Vertical(g3)
    c: DistanceX(g0,g0) = 65
    c: DistanceY(g1,g1) = 30
    c: Symmetric(g0,g0,g-2)
    c: Symmetric(g0,g1,g-1)
    c: Coincident(g4,g5)
    c: Coincident(g5,g6)
    c: Coincident(g6,g7)
    c: Coincident(g7,g4)
    c: Horizontal(g4)
    c: Horizontal(g6)
    c: Vertical(g5)
    c: Vertical(g7)
    c: DistanceX(g4,g4) = 58
    c: DistanceY(g5,g5) = 23
    c: Symmetric(g4,g5,g-1)
    c: Symmetric(g4,g4,g-2)
    c: Coincident(g8,g4)
    c: Coincident(g9,g4)
    c: Coincident(g10,g5)
    c: Coincident(g11,g6)
    c: Radius(g11) = 1.375
    c: Radius(g8) = 1.375
    c: Radius(g9) = 1.375
    c: Radius(g10) = 1.375
    c: Coincident(g12,g13)
    c: Coincident(g13,g14)
    c: Coincident(g14,g15)
    c: Coincident(g15,g12)
    c: Horizontal(g12)
    c: Horizontal(g14)
    c: Vertical(g13)
    c: Vertical(g15)
    c: DistanceX(g4,g12) = 0.5
    c: DistanceY(g4,g12) = 0.5
    c: DistanceY(g13,g5) = 0.5
    c: DistanceX(g14,g6) = 0.5
    c: Coincident(g16,g12)
    c: Radius(g16) = 3
    c: Coincident(g17,g12)
    c: Radius(g17) = 3
    c: Coincident(g18,g13)
    c: Radius(g18) = 3
    c: Coincident(g19,g14)
    c: Radius(g19) = 3
    c: PointOnObject(g16,g0)
    c: PointOnObject(g17,g1)
    c: PointOnObject(g18,g2)
    c: PointOnObject(g19,g3)
    c: Coincident(g20,g16)
    c: Horizontal(g20)
    c: Coincident(g20,g17)
    c: Coincident(g21,g17)
    c: Vertical(g21)
    c: Coincident(g18,g21)
    c: Coincident(g22,g18)
    c: Horizontal(g22)
    c: Coincident(g19,g22)
    c: Coincident(g23,g19)
    c: Vertical(g23)
    c: Coincident(g23,g16)
    c: Coincident(g24,g12)
    c: Radius(g24) = 3.3
    c: Coincident(g25,g12)
    c: Radius(g25) = 3.3
    c: Coincident(g26,g13)
    c: Radius(g26) = 3.3
    c: Coincident(g27,g14)
    c: Radius(g27) = 3.3
    c: Vertical(g28)
    c: DistanceX(g28,g2) = 0.3
    c: Coincident(g27,g28)
    c: Coincident(g28,g24)
    c: Horizontal(g29)
    c: DistanceY(g0,g29) = 0.3
    c: Coincident(g24,g29)
    c: Coincident(g25,g29)
    c: Vertical(g30)
    c: DistanceX(g0,g30) = 0.3
    c: Coincident(g25,g30)
    c: Coincident(g30,g26)
    c: Horizontal(g31)
    c: DistanceY(g31,g1) = 0.3
    c: Coincident(g31,g26)
    c: Coincident(g31,g27)
    c: Coincident(g32,g33)
    c: Coincident(g33,g34)
    c: Coincident(g34,g35)
    c: Coincident(g35,g32)
    c: Horizontal(g32)
    c: Horizontal(g34)
    c: Vertical(g33)
    c: Vertical(g35)
    c: DistanceY(g25,g32) = 2
    c: DistanceX(g25,g32) = 2
    c: DistanceY(g33,g26) = 2
    c: DistanceX(g34,g27) = 2
    c: Coincident(g36,g32)
    c: Coincident(g37,g33)
    c: Coincident(g38,g34)
    c: Coincident(g39,g32)
    c: Radius(g39) = 5
    c: Radius(g38) = 5
    c: Radius(g37) = 5
    c: Radius(g36) = 5
    c: Radius(g40) = 3
    c: Tangent(g40,g36)
    c: Tangent(g40,g32)
    c: Tangent(g47,g36)
    c: Radius(g47) = 3
    c: Tangent(g47,g33)
    c: Radius(g46) = 3
    c: Tangent(g46,g37)
    c: Tangent(g46,g33)
    c: Radius(g45) = 3
    c: Tangent(g45,g37)
    c: Tangent(g45,g34)
    c: Radius(g44) = 3
    c: Tangent(g44,g34)
    c: Tangent(g44,g38)
    c: Radius(g43) = 3
    c: Tangent(g43,g38)
    c: Tangent(g43,g35)
    c: Radius(g42) = 3
    c: Tangent(g42,g35)
    c: Tangent(g42,g39)
    c: Radius(g41) = 3
    c: Tangent(g41,g32)
    c: Tangent(g41,g39)
    c: Coincident(g48,g32)
    c: PointOnObject(g48,g36)
    c: Coincident(g49,g40)
    c: PointOnObject(g49,g40)
    c: Coincident(g50,g47)
    c: PointOnObject(g50,g47)
    c: Coincident(g51,g46)
    c: PointOnObject(g51,g46)
    c: Coincident(g52,g33)
    c: PointOnObject(g52,g37)
    c: Coincident(g53,g45)
    c: PointOnObject(g53,g45)
    c: Coincident(g54,g44)
    c: PointOnObject(g54,g44)
    c: Coincident(g55,g34)
    c: PointOnObject(g55,g38)
    c: Coincident(g56,g43)
    c: PointOnObject(g56,g43)
    c: Coincident(g57,g42)
    c: PointOnObject(g57,g42)
    c: Coincident(g58,g32)
    c: PointOnObject(g58,g39)
    c: Coincident(g59,g41)
    c: PointOnObject(g59,g41)
    c: Coincident(g49,g48)
    c: Coincident(g48,g50)
    c: Coincident(g51,g52)
    c: Coincident(g52,g53)
    c: Coincident(g54,g55)
    c: Coincident(g55,g56)
    c: Coincident(g57,g58)
    c: Coincident(g58,g59)
    c: PointOnObject(g60,g32)
    c: Horizontal(g60)
    c: PointOnObject(g61,g33)
    c: Vertical(g61)
    c: PointOnObject(g62,g34)
    c: Horizontal(g62)
    c: PointOnObject(g63,g35)
    c: Vertical(g63)
    c: Coincident(g59,g60)
    c: Coincident(g60,g49)
    c: Coincident(g50,g61)
    c: Coincident(g61,g51)
    c: Coincident(g53,g62)
    c: Coincident(g54,g62)
    c: Coincident(g56,g63)
    c: Coincident(g57,g63)
    c: Coincident(g64,g4)
    c: Radius(g64) = 3
    c: Coincident(g65,g12)
    c: PointOnObject(g66,g29)
    c: Horizontal(g66)
    c: Coincident(g65,g66)
    c: PointOnObject(g65,g25)
    c: PointOnObject(g67,g30)
    c: Vertical(g67)
    c: Coincident(g67,g65)
    c: Vertical(g68)
    c: Coincident(g68,g64)
    c: Coincident(g68,g66)
    c: Horizontal(g69)
    c: Coincident(g64,g69)
    c: Coincident(g67,g69)
    c: PointOnObject(g70,g-1)
    c: Horizontal(g70)
    c: PointOnObject(g71,g-2)
    c: Vertical(g71)
    c: Radius(g73) = 3
    c: Horizontal(g75)
    c: Coincident(g76,g75)
    c: Vertical(g77)
    c: Coincident(g77,g76)
    c: Vertical(g72)
    c: Coincident(g72,g73)
    c: Coincident(g72,g75)
    c: Horizontal(g74)
    c: Coincident(g73,g74)
    c: Coincident(g77,g74)
    c: Radius(g89) = 3
    c: Horizontal(g87)
    c: Coincident(g86,g87)
    c: Vertical(g85)
    c: Coincident(g85,g86)
    c: Vertical(g88)
    c: Coincident(g88,g89)
    c: Coincident(g88,g87)
    c: Horizontal(g84)
    c: Coincident(g89,g84)
    c: Coincident(g85,g84)
    c: Radius(g83) = 3
    c: Horizontal(g81)
    c: Coincident(g80,g81)
    c: Vertical(g79)
    c: Coincident(g79,g80)
    c: Vertical(g82)
    c: Coincident(g82,g83)
    c: Coincident(g82,g81)
    c: Horizontal(g78)
    c: Coincident(g83,g78)
    c: Coincident(g79,g78)
    c: Coincident(g90,g4)
    c: Radius(g90) = 0.5
    c: Coincident(g91,g6)
    c: Radius(g91) = 0.5
FEATURE [PartDesign::Pad] Pad001
  BaseFeature = -> Pocket
  Length = 2
  Length2 = 100
  Profile = -> Sketch003
  Type = 0
FEATURE [Sketcher::SketchObject] Sketch004
  MapMode = 5
  Placement = pos=(0,0,8.5) rot=(0,0,1;0rad)
  Support = -> [Pad001]
  expr: Constraints[133] = Sketch001.Constraints[133]
  expr: Constraints[130] = Sketch001.Constraints[130]
  expr: Constraints[112] = Sketch001.Constraints[112]
  expr: Constraints[124] = Sketch001.Constraints[124]
  expr: Constraints[127] = Sketch001.Constraints[127]
  expr: Constraints[110] = Sketch001.Constraints[110]
  expr: Constraints[51] = Sketch001.Constraints[51]
  expr: Constraints[100] = Sketch001.Constraints[100]
  expr: Constraints[77] = Sketch001.Constraints[77]
  expr: Constraints[89] = Sketch001.Constraints[89]
  expr: Constraints[85] = Sketch001.Constraints[85]
  expr: Constraints[118] = Sketch001.Constraints[118]
  expr: Constraints[71] = Sketch001.Constraints[71]
  expr: Constraints[111] = Sketch001.Constraints[111]
  expr: Constraints[103] = Sketch001.Constraints[103]
  expr: Constraints[49] = Sketch001.Constraints[49]
  expr: Constraints[102] = Sketch001.Constraints[102]
  expr: Constraints[69] = Sketch001.Constraints[69]
  expr: Constraints[47] = Sketch001.Constraints[47]
  expr: Constraints[73] = Sketch001.Constraints[73]
  expr: Constraints[75] = Sketch001.Constraints[75]
  expr: Constraints[31] = Sketch001.Constraints[31]
  expr: Constraints[116] = Sketch001.Constraints[116]
  expr: Constraints[40] = Sketch001.Constraints[40]
  expr: Constraints[30] = Sketch001.Constraints[30]
  expr: Constraints[29] = Sketch001.Constraints[29]
  expr: Constraints[28] = Sketch001.Constraints[28]
  expr: Constraints[121] = Sketch001.Constraints[121]
  expr: Constraints[21] = Sketch001.Constraints[21]
  expr: Constraints[20] = Sketch001.Constraints[20]
  expr: Constraints[42] = Sketch001.Constraints[42]
  expr: Constraints[43] = Sketch001.Constraints[43]
  expr: Constraints[101] = Sketch001.Constraints[101]
  expr: Constraints[45] = Sketch001.Constraints[45]
  expr: Constraints[108] = Sketch001.Constraints[108]
  expr: Constraints[41] = Sketch001.Constraints[41]
  expr: Constraints[9] = Sketch001.Constraints[9]
  expr: Constraints[81] = Sketch001.Constraints[81]
  expr: Constraints[109] = Sketch001.Constraints[109]
  expr: Constraints[8] = Sketch001.Constraints[8]
  sketch-geometry (68):
    g0: LineSegment [constr] StartX=-32.5 StartY=15 StartZ=0 EndX=32.5 EndY=15 EndZ=0
    g1: LineSegment [constr] StartX=32.5 StartY=15 StartZ=0 EndX=32.5 EndY=-15 EndZ=0
    g2: LineSegment [constr] StartX=32.5 StartY=-15 StartZ=0 EndX=-32.5 EndY=-15 EndZ=0
    g3: LineSegment [constr] StartX=-32.5 StartY=-15 StartZ=0 EndX=-32.5 EndY=15 EndZ=0
    g4: LineSegment [constr] StartX=-29 StartY=11.5 StartZ=0 EndX=29 EndY=11.5 EndZ=0
    g5: LineSegment [constr] StartX=29 StartY=11.5 StartZ=0 EndX=29 EndY=-11.5 EndZ=0
    g6: LineSegment [constr] StartX=29 StartY=-11.5 StartZ=0 EndX=-29 EndY=-11.5 EndZ=0
    g7: LineSegment [constr] StartX=-29 StartY=-11.5 StartZ=0 EndX=-29 EndY=11.5 EndZ=0
    g8: Circle [constr] CenterX=-29 CenterY=11.5 CenterZ=0 NormalX=0 NormalY=0 NormalZ=1 AngleXU=0 Radius=1.375
    g9: Circle [constr] CenterX=29 CenterY=11.5 CenterZ=0 NormalX=0 NormalY=0 NormalZ=1 AngleXU=0 Radius=1.375
    g10: Circle [constr] CenterX=29 CenterY=-11.5 CenterZ=0 NormalX=0 NormalY=0 NormalZ=1 AngleXU=0 Radius=1.375
    g11: Circle [constr] CenterX=-29 CenterY=-11.5 CenterZ=0 NormalX=0 NormalY=0 NormalZ=1 AngleXU=0 Radius=1.375
    g12: LineSegment [constr] StartX=-29.5 StartY=12 StartZ=0 EndX=29.5 EndY=12 EndZ=0
    g13: LineSegment [constr] StartX=29.5 StartY=12 StartZ=0 EndX=29.5 EndY=-12 EndZ=0
    g14: LineSegment [constr] StartX=29.5 StartY=-12 StartZ=0 EndX=-29.5 EndY=-12 EndZ=0
    g15: LineSegment [constr] StartX=-29.5 StartY=-12 StartZ=0 EndX=-29.5 EndY=12 EndZ=0
    g16: ArcOfCircle [constr] CenterX=-29.5 CenterY=12 CenterZ=0 NormalX=0 NormalY=0 NormalZ=1 AngleXU=0 Radius=3 StartAngle=1.5708 EndAngle=3.14159
    g17: ArcOfCircle [constr] CenterX=29.5 CenterY=12 CenterZ=0 NormalX=0 NormalY=0 NormalZ=1 AngleXU=0 Radius=3 StartAngle=2.8425e-08 EndAngle=1.5708
    g18: ArcOfCircle [constr] CenterX=29.5 CenterY=-12 CenterZ=0 NormalX=0 NormalY=0 NormalZ=1 AngleXU=0 Radius=3 StartAngle=4.71239 EndAngle=6.28319
    g19: ArcOfCircle [constr] CenterX=-29.5 CenterY=-12 CenterZ=0 NormalX=0 NormalY=0 NormalZ=1 AngleXU=0 Radius=3 StartAngle=3.14159 EndAngle=4.71239
    g20: LineSegment [constr] StartX=-29.5 StartY=15 StartZ=0 EndX=29.5 EndY=15 EndZ=0
    g21: LineSegment [constr] StartX=32.5 StartY=12 StartZ=0 EndX=32.5 EndY=-12 EndZ=0
    g22: LineSegment [constr] StartX=29.5 StartY=-15 StartZ=0 EndX=-29.5 EndY=-15 EndZ=0
    g23: LineSegment [constr] StartX=-32.5 StartY=-12 StartZ=0 EndX=-32.5 EndY=12 EndZ=0
    g24: ArcOfCircle [constr] CenterX=-29.5 CenterY=12 CenterZ=0 NormalX=0 NormalY=0 NormalZ=1 AngleXU=0 Radius=3.3 StartAngle=1.5708 EndAngle=3.14159
    g25: ArcOfCircle [constr] CenterX=29.5 CenterY=12 CenterZ=0 NormalX=0 NormalY=0 NormalZ=1 AngleXU=0 Radius=3.3 StartAngle=-2.2e-10 EndAngle=1.5708
    g26: ArcOfCircle [constr] CenterX=29.5 CenterY=-12 CenterZ=0 NormalX=0 NormalY=0 NormalZ=1 AngleXU=0 Radius=3.3 StartAngle=4.71239 EndAngle=6.28319
    g27: ArcOfCircle [constr] CenterX=-29.5 CenterY=-12 CenterZ=0 NormalX=0 NormalY=0 NormalZ=1 AngleXU=0 Radius=3.3 StartAngle=3.14159 EndAngle=4.71239
    g28: LineSegment [constr] StartX=-32.8 StartY=12 StartZ=0 EndX=-32.8 EndY=-12 EndZ=0
    g29: LineSegment [constr] StartX=-29.5 StartY=15.3 StartZ=0 EndX=29.5 EndY=15.3 EndZ=0
    g30: LineSegment [constr] StartX=32.8 StartY=12 StartZ=0 EndX=32.8 EndY=-12 EndZ=0
    g31: LineSegment [constr] StartX=29.5 StartY=-15.3 StartZ=0 EndX=-29.5 EndY=-15.3 EndZ=0
    g32: LineSegment [constr] StartX=-34.8 StartY=17.3 StartZ=0 EndX=34.8 EndY=17.3 EndZ=0
    g33: LineSegment [constr] StartX=34.8 StartY=17.3 StartZ=0 EndX=34.8 EndY=-17.3 EndZ=0
    g34: LineSegment [constr] StartX=34.8 StartY=-17.3 StartZ=0 EndX=-34.8 EndY=-17.3 EndZ=0
    g35: LineSegment [constr] StartX=-34.8 StartY=-17.3 StartZ=0 EndX=-34.8 EndY=17.3 EndZ=0
    g36: Circle [constr] CenterX=34.8 CenterY=17.3 CenterZ=0 NormalX=0 NormalY=0 NormalZ=1 AngleXU=0 Radius=5
    g37: Circle [constr] CenterX=34.8 CenterY=-17.3 CenterZ=0 NormalX=0 NormalY=0 NormalZ=1 AngleXU=0 Radius=5
    g38: Circle [constr] CenterX=-34.8 CenterY=-17.3 CenterZ=0 NormalX=0 NormalY=0 NormalZ=1 AngleXU=0 Radius=5
    g39: Circle [constr] CenterX=-34.8 CenterY=17.3 CenterZ=0 NormalX=0 NormalY=0 NormalZ=1 AngleXU=0 Radius=5
    g40: Circle [constr] CenterX=27.3838 CenterY=20.3 CenterZ=0 NormalX=0 NormalY=0 NormalZ=1 AngleXU=0 Radius=3
    g41: Circle [constr] CenterX=-27.3838 CenterY=20.3 CenterZ=0 NormalX=0 NormalY=0 NormalZ=1 AngleXU=0 Radius=3
    g42: Circle [constr] CenterX=-37.8 CenterY=9.8838 CenterZ=0 NormalX=0 NormalY=0 NormalZ=1 AngleXU=0 Radius=3
    g43: Circle [constr] CenterX=-37.8 CenterY=-9.8838 CenterZ=0 NormalX=0 NormalY=0 NormalZ=1 AngleXU=0 Radius=3
    g44: Circle [constr] CenterX=-27.3838 CenterY=-20.3 CenterZ=0 NormalX=0 NormalY=0 NormalZ=1 AngleXU=0 Radius=3
    g45: Circle [constr] CenterX=27.3838 CenterY=-20.3 CenterZ=0 NormalX=0 NormalY=0 NormalZ=1 AngleXU=0 Radius=3
    g46: Circle [constr] CenterX=37.8 CenterY=-9.8838 CenterZ=0 NormalX=0 NormalY=0 NormalZ=1 AngleXU=0 Radius=3
    g47: Circle [constr] CenterX=37.8 CenterY=9.8838 CenterZ=0 NormalX=0 NormalY=0 NormalZ=1 AngleXU=0 Radius=3
    g48: ArcOfCircle [constr] CenterX=34.8 CenterY=17.3 CenterZ=0 NormalX=0 NormalY=0 NormalZ=1 AngleXU=0 Radius=5 StartAngle=5.09679 EndAngle=9.04038
    g49: ArcOfCircle [constr] CenterX=27.3838 CenterY=20.3 CenterZ=0 NormalX=0 NormalY=0 NormalZ=1 AngleXU=0 Radius=3 StartAngle=4.71239 EndAngle=5.89879
    g50: ArcOfCircle [constr] CenterX=37.8 CenterY=9.8838 CenterZ=0 NormalX=0 NormalY=0 NormalZ=1 AngleXU=0 Radius=3 StartAngle=1.95519 EndAngle=3.14159
    g51: ArcOfCircle [constr] CenterX=37.8 CenterY=-9.8838 CenterZ=0 NormalX=0 NormalY=0 NormalZ=1 AngleXU=0 Radius=3 StartAngle=3.14159 EndAngle=4.32799
    g52: ArcOfCircle [constr] CenterX=34.8 CenterY=-17.3 CenterZ=0 NormalX=0 NormalY=0 NormalZ=1 AngleXU=0 Radius=5 StartAngle=3.52599 EndAngle=7.46958
    g53: ArcOfCircle [constr] CenterX=27.3838 CenterY=-20.3 CenterZ=0 NormalX=0 NormalY=0 NormalZ=1 AngleXU=0 Radius=3 StartAngle=0.384397 EndAngle=1.5708
    g54: ArcOfCircle [constr] CenterX=-27.3838 CenterY=-20.3 CenterZ=0 NormalX=0 NormalY=0 NormalZ=1 AngleXU=0 Radius=3 StartAngle=1.5708 EndAngle=2.7572
    g55: ArcOfCircle [constr] CenterX=-34.8 CenterY=-17.3 CenterZ=0 NormalX=0 NormalY=0 NormalZ=1 AngleXU=0 Radius=5 StartAngle=1.95519 EndAngle=5.89879
    g56: ArcOfCircle [constr] CenterX=-37.8 CenterY=-9.8838 CenterZ=0 NormalX=0 NormalY=0 NormalZ=1 AngleXU=0 Radius=3 StartAngle=5.09679 EndAngle=6.28319
    g57: ArcOfCircle [constr] CenterX=-37.8 CenterY=9.8838 CenterZ=0 NormalX=0 NormalY=0 NormalZ=1 AngleXU=0 Radius=3 StartAngle=6.28319 EndAngle=7.46958
    g58: ArcOfCircle [constr] CenterX=-34.8 CenterY=17.3 CenterZ=0 NormalX=0 NormalY=0 NormalZ=1 AngleXU=0 Radius=5 StartAngle=0.384397 EndAngle=4.32799
    g59: ArcOfCircle [constr] CenterX=-27.3838 CenterY=20.3 CenterZ=0 NormalX=0 NormalY=0 NormalZ=1 AngleXU=0 Radius=3 StartAngle=3.52599 EndAngle=4.71239
    g60: LineSegment [constr] StartX=-27.3838 StartY=17.3 StartZ=0 EndX=27.3838 EndY=17.3 EndZ=0
    g61: LineSegment [constr] StartX=34.8 StartY=9.8838 StartZ=0 EndX=34.8 EndY=-9.8838 EndZ=0
    g62: LineSegment [constr] StartX=27.3838 StartY=-17.3 StartZ=0 EndX=-27.3838 EndY=-17.3 EndZ=0
    g63: LineSegment [constr] StartX=-34.8 StartY=-9.8838 StartZ=0 EndX=-34.8 EndY=9.8838 EndZ=0
    g64: Circle CenterX=34.8 CenterY=17.3 CenterZ=0 NormalX=0 NormalY=0 NormalZ=1 AngleXU=0 Radius=3.2
    g65: Circle CenterX=34.8 CenterY=-17.3 CenterZ=0 NormalX=0 NormalY=0 NormalZ=1 AngleXU=0 Radius=3.2
    g66: Circle CenterX=-34.8 CenterY=-17.3 CenterZ=0 NormalX=0 NormalY=0 NormalZ=1 AngleXU=0 Radius=3.2
    g67: Circle CenterX=-34.8 CenterY=17.3 CenterZ=0 NormalX=0 NormalY=0 NormalZ=1 AngleXU=0 Radius=3.2
  constraints (192):
    c: Coincident(g0,g1)
    c: Coincident(g1,g2)
    c: Coincident(g2,g3)
    c: Coincident(g3,g0)
    c: Horizontal(g0)
    c: Horizontal(g2)
    c: Vertical(g1)
    c: Vertical(g3)
    c: DistanceX(g0,g0) = 65
    c: DistanceY(g1,g1) = 30
    c: Symmetric(g0,g0,g-2)
    c: Symmetric(g0,g1,g-1)
    c: Coincident(g4,g5)
    c: Coincident(g5,g6)
    c: Coincident(g6,g7)
    c: Coincident(g7,g4)
    c: Horizontal(g4)
    c: Horizontal(g6)
    c: Vertical(g5)
    c: Vertical(g7)
    c: DistanceX(g4,g4) = 58
    c: DistanceY(g5,g5) = 23
    c: Symmetric(g4,g5,g-1)
    c: Symmetric(g4,g4,g-2)
    c: Coincident(g8,g4)
    c: Coincident(g9,g4)
    c: Coincident(g10,g5)
    c: Coincident(g11,g6)
    c: Radius(g11) = 1.375
    c: Radius(g8) = 1.375
    c: Radius(g9) = 1.375
    c: Radius(g10) = 1.375
    c: Coincident(g12,g13)
    c: Coincident(g13,g14)
    c: Coincident(g14,g15)
    c: Coincident(g15,g12)
    c: Horizontal(g12)
    c: Horizontal(g14)
    c: Vertical(g13)
    c: Vertical(g15)
    c: DistanceX(g4,g12) = 0.5
    c: DistanceY(g4,g12) = 0.5
    c: DistanceY(g13,g5) = 0.5
    c: DistanceX(g14,g6) = 0.5
    c: Coincident(g16,g12)
    c: Radius(g16) = 3
    c: Coincident(g17,g12)
    c: Radius(g17) = 3
    c: Coincident(g18,g13)
    c: Radius(g18) = 3
    c: Coincident(g19,g14)
    c: Radius(g19) = 3
    c: PointOnObject(g16,g0)
    c: PointOnObject(g17,g1)
    c: PointOnObject(g18,g2)
    c: PointOnObject(g19,g3)
    c: Coincident(g20,g16)
    c: Horizontal(g20)
    c: Coincident(g20,g17)
    c: Coincident(g21,g17)
    c: Vertical(g21)
    c: Coincident(g18,g21)
    c: Coincident(g22,g18)
    c: Horizontal(g22)
    c: Coincident(g19,g22)
    c: Coincident(g23,g19)
    c: Vertical(g23)
    c: Coincident(g23,g16)
    c: Coincident(g24,g12)
    c: Radius(g24) = 3.3
    c: Coincident(g25,g12)
    c: Radius(g25) = 3.3
    c: Coincident(g26,g13)
    c: Radius(g26) = 3.3
    c: Coincident(g27,g14)
    c: Radius(g27) = 3.3
    c: Vertical(g28)
    c: DistanceX(g28,g2) = 0.3
    c: Coincident(g27,g28)
    c: Coincident(g28,g24)
    c: Horizontal(g29)
    c: DistanceY(g0,g29) = 0.3
    c: Coincident(g24,g29)
    c: Coincident(g25,g29)
    c: Vertical(g30)
    c: DistanceX(g0,g30) = 0.3
    c: Coincident(g25,g30)
    c: Coincident(g30,g26)
    c: Horizontal(g31)
    c: DistanceY(g31,g1) = 0.3
    c: Coincident(g31,g26)
    c: Coincident(g31,g27)
    c: Coincident(g32,g33)
    c: Coincident(g33,g34)
    c: Coincident(g34,g35)
    c: Coincident(g35,g32)
    c: Horizontal(g32)
    c: Horizontal(g34)
    c: Vertical(g33)
    c: Vertical(g35)
    c: DistanceY(g25,g32) = 2
    c: DistanceX(g25,g32) = 2
    c: DistanceY(g33,g26) = 2
    c: DistanceX(g34,g27) = 2
    c: Coincident(g36,g32)
    c: Coincident(g37,g33)
    c: Coincident(g38,g34)
    c: Coincident(g39,g32)
    c: Radius(g39) = 5
    c: Radius(g38) = 5
    c: Radius(g37) = 5
    c: Radius(g36) = 5
    c: Radius(g40) = 3
    c: Tangent(g40,g36)
    c: Tangent(g40,g32)
    c: Tangent(g47,g36)
    c: Radius(g47) = 3
    c: Tangent(g47,g33)
    c: Radius(g46) = 3
    c: Tangent(g46,g37)
    c: Tangent(g46,g33)
    c: Radius(g45) = 3
    c: Tangent(g45,g37)
    c: Tangent(g45,g34)
    c: Radius(g44) = 3
    c: Tangent(g44,g34)
    c: Tangent(g44,g38)
    c: Radius(g43) = 3
    c: Tangent(g43,g38)
    c: Tangent(g43,g35)
    c: Radius(g42) = 3
    c: Tangent(g42,g35)
    c: Tangent(g42,g39)
    c: Radius(g41) = 3
    c: Tangent(g41,g32)
    c: Tangent(g41,g39)
    c: Coincident(g48,g32)
    c: PointOnObject(g48,g36)
    c: Coincident(g49,g40)
    c: PointOnObject(g49,g40)
    c: Coincident(g50,g47)
    c: PointOnObject(g50,g47)
    c: Coincident(g51,g46)
    c: PointOnObject(g51,g46)
    c: Coincident(g52,g33)
    c: PointOnObject(g52,g37)
    c: Coincident(g53,g45)
    c: PointOnObject(g53,g45)
    c: Coincident(g54,g44)
    c: PointOnObject(g54,g44)
    c: Coincident(g55,g34)
    c: PointOnObject(g55,g38)
    c: Coincident(g56,g43)
    c: PointOnObject(g56,g43)
    c: Coincident(g57,g42)
    c: PointOnObject(g57,g42)
    c: Coincident(g58,g32)
    c: PointOnObject(g58,g39)
    c: Coincident(g59,g41)
    c: PointOnObject(g59,g41)
    c: Coincident(g49,g48)
    c: Coincident(g48,g50)
    c: Coincident(g51,g52)
    c: Coincident(g52,g53)
    c: Coincident(g54,g55)
    c: Coincident(g55,g56)
    c: Coincident(g57,g58)
    c: Coincident(g58,g59)
    c: PointOnObject(g60,g32)
    c: Horizontal(g60)
    c: PointOnObject(g61,g33)
    c: Vertical(g61)
    c: PointOnObject(g62,g34)
    c: Horizontal(g62)
    c: PointOnObject(g63,g35)
    c: Vertical(g63)
    c: Coincident(g59,g60)
    c: Coincident(g60,g49)
    c: Coincident(g50,g61)
    c: Coincident(g61,g51)
    c: Coincident(g53,g62)
    c: Coincident(g54,g62)
    c: Coincident(g56,g63)
    c: Coincident(g57,g63)
    c: Coincident(g64,g32)
    c: Coincident(g65,g33)
    c: Coincident(g66,g34)
    c: Coincident(g67,g32)
    c: Radius(g67) = 3.2
    c: Radius(g64) = 3.2
    c: Radius(g65) = 3.2
    c: Radius(g66) = 3.2
FEATURE [PartDesign::Pad] Pad002
  BaseFeature = -> Pad001
  Length = 2
  Length2 = 100
  Profile = -> Sketch004
  Type = 0
FEATURE [Sketcher::SketchObject] Sketch005
  MapMode = 5
  Placement = pos=(0,-17.3,-3.5) rot=(1,0,0;1.5708rad)
  sketch-geometry (22):
    g0: LineSegment StartX=-26.0242 StartY=12 StartZ=0 EndX=-14.2242 EndY=12 EndZ=0
    g1: LineSegment StartX=-14.2242 StartY=12 StartZ=0 EndX=-14.2242 EndY=9.7 EndZ=0
    g2: LineSegment StartX=-26.0242 StartY=9.7 StartZ=0 EndX=-26.0242 EndY=12 EndZ=0
    g3: LineSegment [constr] StartX=-20.1242 StartY=16.7174 StartZ=0 EndX=-20.1242 EndY=2.05389 EndZ=0
    g4: LineSegment [constr] StartX=-26 StartY=7.5 StartZ=0 EndX=23.454 EndY=7.5 EndZ=0
    g5: LineSegment StartX=-24.5941 StartY=8.5 StartZ=0 EndX=-15.6543 EndY=8.5 EndZ=0
    g6: LineSegment StartX=-26.0242 StartY=9.7 StartZ=0 EndX=-24.5941 EndY=8.5 EndZ=0
    g7: LineSegment StartX=-15.6543 StartY=8.5 StartZ=0 EndX=-14.2242 EndY=9.7 EndZ=0
    g8: LineSegment StartX=4.8858 StartY=12 StartZ=0 EndX=12.8858 EndY=12 EndZ=0
    g9: LineSegment StartX=12.8858 StartY=12 StartZ=0 EndX=12.8858 EndY=9.28 EndZ=0
    g10: LineSegment StartX=4.8858 StartY=9.28 StartZ=0 EndX=4.8858 EndY=12 EndZ=0
    g11: LineSegment [constr] StartX=8.8858 StartY=17.7004 StartZ=0 EndX=8.8858 EndY=3.91586 EndZ=0
    g12: LineSegment StartX=4.8858 StartY=9.28 StartZ=0 EndX=5.8858 EndY=8.28 EndZ=0
    g13: LineSegment StartX=11.8858 StartY=8.28 StartZ=0 EndX=12.8858 EndY=9.28 EndZ=0
    g14: LineSegment StartX=5.8858 StartY=8.28 StartZ=0 EndX=11.8858 EndY=8.28 EndZ=0
    g15: LineSegment StartX=17.5058 StartY=12 StartZ=0 EndX=25.5058 EndY=12 EndZ=0
    g16: LineSegment StartX=25.5058 StartY=12 StartZ=0 EndX=25.5058 EndY=9.28 EndZ=0
    g17: LineSegment StartX=17.5058 StartY=9.28 StartZ=0 EndX=17.5058 EndY=12 EndZ=0
    g18: LineSegment StartX=17.5058 StartY=9.28 StartZ=0 EndX=18.5058 EndY=8.28 EndZ=0
    g19: LineSegment StartX=24.5058 StartY=8.28 StartZ=0 EndX=25.5058 EndY=9.28 EndZ=0
    g20: LineSegment StartX=18.5058 StartY=8.28 StartZ=0 EndX=24.5058 EndY=8.28 EndZ=0
    g21: LineSegment [constr] StartX=21.5058 StartY=16.2884 StartZ=0 EndX=21.5058 EndY=2.78996 EndZ=0
  constraints (57):
    c: Coincident(g0,g1)
    c: Coincident(g2,g0)
    c: Horizontal(g0)
    c: Vertical(g1)
    c: Vertical(g2)
    c: Vertical(g3)
    c: Symmetric(g0,g0,g3)
    c: DistanceX(g0,g0) = 11.8
    c: Horizontal(g4)
    c: Horizontal(g5)
    c: Angle(g5,g6) = 2.44346
    c: Angle(g7,g5) = 2.44346
    c: Coincident(g2,g6)
    c: Coincident(g6,g5)
    c: DistanceY(g5,g2) = 1.2
    c: Coincident(g7,g5)
    c: DistanceY(g5,g7) = 1.2
    c: Coincident(g1,g7)
    c: DistanceY(g4,g5) = 1
    c: Coincident(g8,g9)
    c: Coincident(g10,g8)
    c: Horizontal(g8)
    c: Vertical(g9)
    c: Vertical(g10)
    c: DistanceX(g8,g8) = 8
    c: Vertical(g11)
    c: DistanceX(g3,g11) = 29.01
    c: Symmetric(g8,g8,g11)
    c: Horizontal(g14)
    c: DistanceY(g4,g14) = 0.78
    c: Angle(g13,g14) = 2.35619
    c: Angle(g14,g12) = 2.35619
    c: Coincident(g12,g14)
    c: Coincident(g12,g10)
    c: DistanceY(g12,g10) = 1
    c: Coincident(g14,g13)
    c: Coincident(g13,g9)
    c: DistanceY(g13,g9) = 1
    c: Coincident(g15,g16)
    c: Coincident(g17,g15)
    c: Horizontal(g15)
    c: Vertical(g16)
    c: Vertical(g17)
    c: Equal(g8,g15) = 7.8
    c: Horizontal(g20)
    c: Angle(g19,g20) = 2.35619
    c: Angle(g20,g18) = 2.35619
    c: Coincident(g18,g20)
    c: Coincident(g18,g17)
    c: DistanceY(g18,g17) = 1
    c: Coincident(g20,g19)
    c: Coincident(g19,g16)
    c: DistanceY(g19,g16) = 1
    c: DistanceY(g4,g18) = 0.78
    c: Vertical(g21)
    c: DistanceX(g11,g21) = 12.62
    c: Symmetric(g15,g15,g21)
FEATURE [PartDesign::Pocket] Pocket002
  BaseFeature = -> Pad002
  Length = 5
  Length2 = 100
  Profile = -> Sketch005
  Type = 2
FEATURE [Sketcher::SketchObject] Sketch006
  AttachmentOffset = pos=(0,-3.5,0) rot=(0,0,1;0rad)
  ExternalGeometry = -> [Pocket002]
  MapMode = 5
  Placement = pos=(-34.8,0,-3.5) rot=(0.57735,-0.57735,-0.57735;2.0944rad)
  Support = -> [Pocket002]
  sketch-geometry (12):
    g0: LineSegment [constr] StartX=-8.50001 StartY=7.5 StartZ=0 EndX=0.928937 EndY=7.5 EndZ=0
    g1: LineSegment [constr] StartX=-1.67421 StartY=13.4438 StartZ=0 EndX=-1.67421 EndY=3.80207 EndZ=0
    g2: LineSegment [constr] StartX=-11.4942 StartY=7.5 StartZ=0 EndX=-11.4942 EndY=14.033 EndZ=0
    g3: LineSegment StartX=4.62579 StartY=10.3 StartZ=0 EndX=4.62579 EndY=8.5 EndZ=0
    g4: LineSegment StartX=4.62579 StartY=8.5 StartZ=0 EndX=-7.97421 EndY=8.5 EndZ=0
    g5: LineSegment StartX=-7.97421 StartY=8.5 StartZ=0 EndX=-7.97421 EndY=10.3 EndZ=0
    g6: LineSegment [constr] StartX=4.62579 StartY=10.3 StartZ=0 EndX=-7.97421 EndY=10.3 EndZ=0
    g7: ArcOfEllipse CenterX=-1.67421 CenterY=10.3 CenterZ=0 NormalX=0 NormalY=0 NormalZ=1 MajorRadius=6.3 MinorRadius=1.00676 AngleXU=-3.14159 StartAngle=3.14159 EndAngle=6.28319
    g8: LineSegment [constr] StartX=-7.97421 StartY=10.3 StartZ=0 EndX=4.62579 EndY=10.3 EndZ=0
    g9: LineSegment [constr] StartX=-1.67421 StartY=9.29324 StartZ=0 EndX=-1.67421 EndY=11.3068 EndZ=0
    g10: GeomPoint X=-7.89325 Y=10.3 Z=0
    g11: GeomPoint X=4.54482 Y=10.3 Z=0
FEATURE [PartDesign::Pocket] Pocket003
  BaseFeature = -> Pocket002
  Length = 5
  Length2 = 100
  Profile = -> Sketch006
  Type = 2
FEATURE [PartDesign::Chamfer] Chamfer
  Base = -> Pocket003 [Edge60,Edge62]
  BaseFeature = -> Pocket003
  Size = 0.6
FEATURE [Sketcher::SketchObject] Sketch007
  ExternalGeometry = -> [Chamfer]
  MapMode = 5
  Placement = pos=(0,0,10.5) rot=(0,0,1;0rad)
  Support = -> [Chamfer]
  sketch-geometry (4):
    g0: Circle CenterX=34.8 CenterY=17.3 CenterZ=0 NormalX=0 NormalY=0 NormalZ=1 AngleXU=0 Radius=2.43827
    g1: Circle CenterX=-34.8 CenterY=17.3 CenterZ=0 NormalX=0 NormalY=0 NormalZ=1 AngleXU=0 Radius=2.44385
    g2: Circle CenterX=-34.8 CenterY=-17.3 CenterZ=0 NormalX=0 NormalY=0 NormalZ=1 AngleXU=0 Radius=2.67402
    g3: Circle CenterX=34.8 CenterY=-17.3 CenterZ=0 NormalX=0 NormalY=0 NormalZ=1 AngleXU=0 Radius=2.67742
  constraints (4):
    c: Coincident(g0,g-3)
    c: Coincident(g1,g-4)
    c: Coincident(g2,g-6)
    c: Coincident(g3,g-5)
FEATURE [PartDesign::Hole] Hole
  BaseFeature = -> Chamfer
  Depth = 25
  DepthType = 1
  Diameter = 3.3
  DrillPoint = 1
  DrillPointAngle = 118
  HoleCutCountersinkAngle = 90
  HoleCutDepth = 0
  HoleCutDiameter = 3
  HoleCutType = 0
  ModelActualThread = false
  Profile = -> Sketch007
  Tapered = false
  TaperedAngle = 90
  ThreadAngle = 0
  ThreadClass = 0
  ThreadCutOffInner = 0
  ThreadCutOffOuter = 0
  ThreadDirection = 0
  ThreadFit = 0
  ThreadPitch = 0
  ThreadSize = 3
  ThreadType = 1
  Threaded = false
FEATURE [Sketcher::SketchObject] Sketch008
  ExternalGeometry = -> [Hole]
  MapMode = 5
  Placement = pos=(0,0,0) rot=(1,0,0;3.14159rad)
  Support = -> [Hole]
  sketch-geometry (32):
    g0: LineSegment [constr] StartX=-34.8 StartY=27.181 StartZ=0 EndX=-34.8 EndY=-26.8986 EndZ=0
    g1: LineSegment [constr] StartX=34.8 StartY=-24.6336 StartZ=0 EndX=34.8 EndY=23.8401 EndZ=0
    g2: LineSegment [constr] StartX=-45.3318 StartY=17.3 StartZ=0 EndX=42.1188 EndY=17.3 EndZ=0
    g3: LineSegment [constr] StartX=-44.7382 StartY=-17.3 StartZ=0 EndX=39.4916 EndY=-17.3 EndZ=0
    g4: LineSegment StartX=34.8 StartY=14.1708 StartZ=0 EndX=37.51 EndY=15.7354 EndZ=0
    g5: LineSegment StartX=37.51 StartY=15.7354 StartZ=0 EndX=37.51 EndY=18.8646 EndZ=0
    g6: LineSegment StartX=37.51 StartY=18.8646 StartZ=0 EndX=34.8 EndY=20.4292 EndZ=0
    g7: LineSegment StartX=34.8 StartY=20.4292 StartZ=0 EndX=32.09 EndY=18.8646 EndZ=0
    g8: LineSegment StartX=32.09 StartY=18.8646 StartZ=0 EndX=32.09 EndY=15.7354 EndZ=0
    g9: LineSegment StartX=32.09 StartY=15.7354 StartZ=0 EndX=34.8 EndY=14.1708 EndZ=0
    g10: Circle [constr] CenterX=34.8 CenterY=17.3 CenterZ=0 NormalX=0 NormalY=0 NormalZ=1 AngleXU=0 Radius=3.12924
    g11: LineSegment StartX=-34.8 StartY=14.1708 StartZ=0 EndX=-32.09 EndY=15.7354 EndZ=0
    g12: LineSegment StartX=-32.09 StartY=15.7354 StartZ=0 EndX=-32.09 EndY=18.8646 EndZ=0
    g13: LineSegment StartX=-32.09 StartY=18.8646 StartZ=0 EndX=-34.8 EndY=20.4292 EndZ=0
    g14: LineSegment StartX=-34.8 StartY=20.4292 StartZ=0 EndX=-37.51 EndY=18.8646 EndZ=0
    g15: LineSegment StartX=-37.51 StartY=18.8646 StartZ=0 EndX=-37.51 EndY=15.7354 EndZ=0
    g16: LineSegment StartX=-37.51 StartY=15.7354 StartZ=0 EndX=-34.8 EndY=14.1708 EndZ=0
    g17: Circle [constr] CenterX=-34.8 CenterY=17.3 CenterZ=0 NormalX=0 NormalY=0 NormalZ=1 AngleXU=0 Radius=3.12924
    g18: LineSegment StartX=34.8 StartY=-20.4292 StartZ=0 EndX=37.51 EndY=-18.8646 EndZ=0
    g19: LineSegment StartX=37.51 StartY=-18.8646 StartZ=0 EndX=37.51 EndY=-15.7354 EndZ=0
    g20: LineSegment StartX=37.51 StartY=-15.7354 StartZ=0 EndX=34.8 EndY=-14.1708 EndZ=0
    g21: LineSegment StartX=34.8 StartY=-14.1708 StartZ=0 EndX=32.09 EndY=-15.7354 EndZ=0
    g22: LineSegment StartX=32.09 StartY=-15.7354 StartZ=0 EndX=32.09 EndY=-18.8646 EndZ=0
    g23: LineSegment StartX=32.09 StartY=-18.8646 StartZ=0 EndX=34.8 EndY=-20.4292 EndZ=0
    g24: Circle [constr] CenterX=34.8 CenterY=-17.3 CenterZ=0 NormalX=0 NormalY=0 NormalZ=1 AngleXU=0 Radius=3.12924
    g25: LineSegment StartX=-34.8 StartY=-20.4292 StartZ=0 EndX=-32.09 EndY=-18.8646 EndZ=0
    g26: LineSegment StartX=-32.09 StartY=-18.8646 StartZ=0 EndX=-32.09 EndY=-15.7354 EndZ=0
    g27: LineSegment StartX=-32.09 StartY=-15.7354 StartZ=0 EndX=-34.8 EndY=-14.1708 EndZ=0
    g28: LineSegment StartX=-34.8 StartY=-14.1708 StartZ=0 EndX=-37.51 EndY=-15.7354 EndZ=0
    g29: LineSegment StartX=-37.51 StartY=-15.7354 StartZ=0 EndX=-37.51 EndY=-18.8646 EndZ=0
    g30: LineSegment StartX=-37.51 StartY=-18.8646 StartZ=0 EndX=-34.8 EndY=-20.4292 EndZ=0
    g31: Circle [constr] CenterX=-34.8 CenterY=-17.3 CenterZ=0 NormalX=0 NormalY=0 NormalZ=1 AngleXU=0 Radius=3.12924
  constraints (72):
    c: Vertical(g0)
    c: Vertical(g1)
    c: Horizontal(g2)
    c: Horizontal(g3)
    c: PointOnObject(g-6,g3)
    c: PointOnObject(g-6,g1)
    c: PointOnObject(g-5,g0)
    c: PointOnObject(g-4,g2)
    c: Coincident(g4,g5)
    c: Coincident(g5,g6)
    c: Coincident(g6,g7)
    c: Coincident(g7,g8)
    c: Coincident(g8,g9)
    c: Coincident(g9,g4)
    c: Equal(g4, g5-g9) x5
    c: PointOnObject(g4,g10)
    c: PointOnObject(g5,g10)
    c: PointOnObject(g6,g10)
    c: PointOnObject(g7,g10)
    c: PointOnObject(g8,g10)
    c: PointOnObject(g9,g10)
    c: Coincident(g10,g-3)
    c: PointOnObject(g9,g1)
    c: DistanceX(g7,g5) = 5.42
    c: Coincident(g11,g12)
    c: Coincident(g12,g13)
    c: Coincident(g13,g14)
    c: Coincident(g14,g15)
    c: Coincident(g15,g16)
    c: Coincident(g16,g11)
    c: Equal(g11, g12-g16) x5
    c: PointOnObject(g11,g17)
    c: PointOnObject(g12,g17)
    c: PointOnObject(g13,g17)
    c: PointOnObject(g14,g17)
    c: PointOnObject(g15,g17)
    c: PointOnObject(g16,g17)
    c: Coincident(g17,g-4)
    c: PointOnObject(g16,g0)
    c: DistanceX(g14,g12) = 5.42
    c: Coincident(g18,g19)
    c: Coincident(g19,g20)
    c: Coincident(g20,g21)
    c: Coincident(g21,g22)
    c: Coincident(g22,g23)
    c: Coincident(g23,g18)
    c: Equal(g18, g19-g23) x5
    c: PointOnObject(g18,g24)
    c: PointOnObject(g19,g24)
    c: PointOnObject(g20,g24)
    c: PointOnObject(g21,g24)
    c: PointOnObject(g22,g24)
    c: PointOnObject(g23,g24)
    c: Coincident(g24,g-6)
    c: PointOnObject(g23,g1)
    c: DistanceX(g21,g19) = 5.42
    c: Coincident(g25,g26)
    c: Coincident(g26,g27)
    c: Coincident(g27,g28)
    c: Coincident(g28,g29)
    c: Coincident(g29,g30)
    c: Coincident(g30,g25)
    c: Equal(g25, g26-g30) x5
    c: PointOnObject(g25,g31)
    c: PointOnObject(g26,g31)
    c: PointOnObject(g27,g31)
    c: PointOnObject(g28,g31)
    c: PointOnObject(g29,g31)
    c: PointOnObject(g30,g31)
    c: PointOnObject(g30,g0)
    c: DistanceX(g28,g26) = 5.42
    c: Coincident(g31,g-5)
FEATURE [PartDesign::Pocket] Pocket004
  BaseFeature = -> Hole
  Length = 5
  Length2 = 100
  Profile = -> Sketch008
  Type = 0
FEATURE [Sketcher::SketchObject] Sketch009
  MapMode = 5
  Placement = pos=(0,0,4) rot=(0,0,1;0rad)
  Support = -> [Pocket004]
  expr: Constraints[51] = Sketch.Constraints[51]
  expr: Constraints[49] = Sketch.Constraints[49]
  expr: Constraints[47] = Sketch.Constraints[47]
  expr: Constraints[40] = Sketch.Constraints[40]
  expr: Constraints[31] = Sketch.Constraints[31]
  expr: Constraints[30] = Sketch.Constraints[30]
  expr: Constraints[29] = Sketch.Constraints[29]
  expr: Constraints[28] = Sketch.Constraints[28]
  expr: Constraints[21] = Sketch.Constraints[21]
  expr: Constraints[20] = Sketch.Constraints[20]
  expr: Constraints[45] = Sketch.Constraints[45]
  expr: Constraints[43] = Sketch.Constraints[43]
  expr: Constraints[42] = Sketch.Constraints[42]
  expr: Constraints[41] = Sketch.Constraints[41]
  expr: Constraints[9] = Sketch.Constraints[9]
  expr: Constraints[8] = Sketch.Constraints[8]
  sketch-geometry (28):
    g0: LineSegment [constr] StartX=-32.5 StartY=15 StartZ=0 EndX=32.5 EndY=15 EndZ=0
    g1: LineSegment [constr] StartX=32.5 StartY=15 StartZ=0 EndX=32.5 EndY=-15 EndZ=0
    g2: LineSegment [constr] StartX=32.5 StartY=-15 StartZ=0 EndX=-32.5 EndY=-15 EndZ=0
    g3: LineSegment [constr] StartX=-32.5 StartY=-15 StartZ=0 EndX=-32.5 EndY=15 EndZ=0
    g4: LineSegment [constr] StartX=-29 StartY=11.5 StartZ=0 EndX=29 EndY=11.5 EndZ=0
    g5: LineSegment [constr] StartX=29 StartY=11.5 StartZ=0 EndX=29 EndY=-11.5 EndZ=0
    g6: LineSegment [constr] StartX=29 StartY=-11.5 StartZ=0 EndX=-29 EndY=-11.5 EndZ=0
    g7: LineSegment [constr] StartX=-29 StartY=-11.5 StartZ=0 EndX=-29 EndY=11.5 EndZ=0
    g8: Circle [constr] CenterX=-29 CenterY=11.5 CenterZ=0 NormalX=0 NormalY=0 NormalZ=1 AngleXU=0 Radius=1.375
    g9: Circle [constr] CenterX=29 CenterY=11.5 CenterZ=0 NormalX=0 NormalY=0 NormalZ=1 AngleXU=0 Radius=1.375
    g10: Circle [constr] CenterX=29 CenterY=-11.5 CenterZ=0 NormalX=0 NormalY=0 NormalZ=1 AngleXU=0 Radius=1.375
    g11: Circle [constr] CenterX=-29 CenterY=-11.5 CenterZ=0 NormalX=0 NormalY=0 NormalZ=1 AngleXU=0 Radius=1.375
    g12: LineSegment [constr] StartX=-29.5 StartY=12 StartZ=0 EndX=29.5 EndY=12 EndZ=0
    g13: LineSegment [constr] StartX=29.5 StartY=12 StartZ=0 EndX=29.5 EndY=-12 EndZ=0
    g14: LineSegment [constr] StartX=29.5 StartY=-12 StartZ=0 EndX=-29.5 EndY=-12 EndZ=0
    g15: LineSegment [constr] StartX=-29.5 StartY=-12 StartZ=0 EndX=-29.5 EndY=12 EndZ=0
    g16: ArcOfCircle [constr] CenterX=-29.5 CenterY=12 CenterZ=0 NormalX=0 NormalY=0 NormalZ=1 AngleXU=0 Radius=3 StartAngle=1.5708 EndAngle=3.14159
    g17: ArcOfCircle [constr] CenterX=29.5 CenterY=12 CenterZ=0 NormalX=0 NormalY=0 NormalZ=1 AngleXU=0 Radius=3 StartAngle=3.7568e-08 EndAngle=1.5708
    g18: ArcOfCircle [constr] CenterX=29.5 CenterY=-12 CenterZ=0 NormalX=0 NormalY=0 NormalZ=1 AngleXU=0 Radius=3 StartAngle=4.71239 EndAngle=6.28319
    g19: ArcOfCircle [constr] CenterX=-29.5 CenterY=-12 CenterZ=0 NormalX=0 NormalY=0 NormalZ=1 AngleXU=0 Radius=3 StartAngle=3.14159 EndAngle=4.71239
    g20: LineSegment [constr] StartX=-29.5 StartY=15 StartZ=0 EndX=29.5 EndY=15 EndZ=0
    g21: LineSegment [constr] StartX=32.5 StartY=12 StartZ=0 EndX=32.5 EndY=-12 EndZ=0
    g22: LineSegment [constr] StartX=29.5 StartY=-15 StartZ=0 EndX=-29.5 EndY=-15 EndZ=0
    g23: LineSegment [constr] StartX=-32.5 StartY=-12 StartZ=0 EndX=-32.5 EndY=12 EndZ=0
    g24: Circle CenterX=-29 CenterY=-11.5 CenterZ=0 NormalX=0 NormalY=0 NormalZ=1 AngleXU=0 Radius=1.07106
    g25: Circle CenterX=29 CenterY=-11.5 CenterZ=0 NormalX=0 NormalY=0 NormalZ=1 AngleXU=0 Radius=1.09378
    g26: Circle CenterX=29 CenterY=11.5 CenterZ=0 NormalX=0 NormalY=0 NormalZ=1 AngleXU=0 Radius=1.14533
    g27: Circle CenterX=-29 CenterY=11.5 CenterZ=0 NormalX=0 NormalY=0 NormalZ=1 AngleXU=0 Radius=1.23522
  constraints (72):
    c: Coincident(g0,g1)
    c: Coincident(g1,g2)
    c: Coincident(g2,g3)
    c: Coincident(g3,g0)
    c: Horizontal(g0)
    c: Horizontal(g2)
    c: Vertical(g1)
    c: Vertical(g3)
    c: DistanceX(g0,g0) = 65
    c: DistanceY(g1,g1) = 30
    c: Symmetric(g0,g0,g-2)
    c: Symmetric(g0,g1,g-1)
    c: Coincident(g4,g5)
    c: Coincident(g5,g6)
    c: Coincident(g6,g7)
    c: Coincident(g7,g4)
    c: Horizontal(g4)
    c: Horizontal(g6)
    c: Vertical(g5)
    c: Vertical(g7)
    c: DistanceX(g4,g4) = 58
    c: DistanceY(g5,g5) = 23
    c: Symmetric(g4,g5,g-1)
    c: Symmetric(g4,g4,g-2)
    c: Coincident(g8,g4)
    c: Coincident(g9,g4)
    c: Coincident(g10,g5)
    c: Coincident(g11,g6)
    c: Radius(g11) = 1.375
    c: Radius(g8) = 1.375
    c: Radius(g9) = 1.375
    c: Radius(g10) = 1.375
    c: Coincident(g12,g13)
    c: Coincident(g13,g14)
    c: Coincident(g14,g15)
    c: Coincident(g15,g12)
    c: Horizontal(g12)
    c: Horizontal(g14)
    c: Vertical(g13)
    c: Vertical(g15)
    c: DistanceX(g4,g12) = 0.5
    c: DistanceY(g4,g12) = 0.5
    c: DistanceY(g13,g5) = 0.5
    c: DistanceX(g14,g6) = 0.5
    c: Coincident(g16,g12)
    c: Radius(g16) = 3
    c: Coincident(g17,g12)
    c: Radius(g17) = 3
    c: Coincident(g18,g13)
    c: Radius(g18) = 3
    c: Coincident(g19,g14)
    c: Radius(g19) = 3
    c: PointOnObject(g16,g0)
    c: PointOnObject(g17,g1)
    c: PointOnObject(g18,g2)
    c: PointOnObject(g19,g3)
    c: Coincident(g20,g16)
    c: Horizontal(g20)
    c: Coincident(g20,g17)
    c: Coincident(g21,g17)
    c: Vertical(g21)
    c: Coincident(g18,g21)
    c: Coincident(g22,g18)
    c: Horizontal(g22)
    c: Coincident(g19,g22)
    c: Coincident(g23,g19)
    c: Vertical(g23)
    c: Coincident(g23,g16)
    c: Coincident(g24,g6)
    c: Coincident(g25,g5)
    c: Coincident(g26,g4)
    c: Coincident(g27,g4)
FEATURE [PartDesign::Hole] Hole001
  BaseFeature = -> Pocket004
  Depth = 25
  DepthType = 1
  Diameter = 2.2
  DrillPoint = 1
  DrillPointAngle = 118
  HoleCutCountersinkAngle = 90
  HoleCutDepth = 0
  HoleCutDiameter = 2
  HoleCutType = 0
  ModelActualThread = false
  Profile = -> Sketch009
  Tapered = false
  TaperedAngle = 90
  ThreadAngle = 60
  ThreadClass = 0
  ThreadCutOffInner = 0.0433013
  ThreadCutOffOuter = 0.0866025
  ThreadDirection = 0
  ThreadFit = 0
  ThreadPitch = 0.4
  ThreadSize = 1
  ThreadType = 1
  Threaded = false
FEATURE [Sketcher::SketchObject] Sketch010
  ExternalGeometry = -> [Hole001]
  MapMode = 5
  Placement = pos=(0,0,0) rot=(1,0,0;3.14159rad)
  Support = -> [Hole001]
  sketch-geometry (32):
    g0: LineSegment [constr] StartX=-29 StartY=20.1024 StartZ=0 EndX=-29 EndY=-21.8008 EndZ=0
    g1: LineSegment [constr] StartX=29 StartY=21.2945 StartZ=0 EndX=29 EndY=-21.3239 EndZ=0
    g2: LineSegment [constr] StartX=-40.5495 StartY=-11.5 StartZ=0 EndX=38.5479 EndY=-11.5 EndZ=0
    g3: LineSegment [constr] StartX=-40.9667 StartY=11.5 StartZ=0 EndX=41.409 EndY=11.5 EndZ=0
    g4: LineSegment StartX=29 StartY=9.13286 StartZ=0 EndX=31.05 EndY=10.3164 EndZ=0
    g5: LineSegment StartX=31.05 StartY=10.3164 StartZ=0 EndX=31.05 EndY=12.6836 EndZ=0
    g6: LineSegment StartX=31.05 StartY=12.6836 StartZ=0 EndX=29 EndY=13.8671 EndZ=0
    g7: LineSegment StartX=29 StartY=13.8671 StartZ=0 EndX=26.95 EndY=12.6836 EndZ=0
    g8: LineSegment StartX=26.95 StartY=12.6836 StartZ=0 EndX=26.95 EndY=10.3164 EndZ=0
    g9: LineSegment StartX=26.95 StartY=10.3164 StartZ=0 EndX=29 EndY=9.13286 EndZ=0
    g10: Circle [constr] CenterX=29 CenterY=11.5 CenterZ=0 NormalX=0 NormalY=0 NormalZ=1 AngleXU=0 Radius=2.36714
    g11: LineSegment StartX=-29 StartY=9.13286 StartZ=0 EndX=-26.95 EndY=10.3164 EndZ=0
    g12: LineSegment StartX=-26.95 StartY=10.3164 StartZ=0 EndX=-26.95 EndY=12.6836 EndZ=0
    g13: LineSegment StartX=-26.95 StartY=12.6836 StartZ=0 EndX=-29 EndY=13.8671 EndZ=0
    g14: LineSegment StartX=-29 StartY=13.8671 StartZ=0 EndX=-31.05 EndY=12.6836 EndZ=0
    g15: LineSegment StartX=-31.05 StartY=12.6836 StartZ=0 EndX=-31.05 EndY=10.3164 EndZ=0
    g16: LineSegment StartX=-31.05 StartY=10.3164 StartZ=0 EndX=-29 EndY=9.13286 EndZ=0
    g17: Circle [constr] CenterX=-29 CenterY=11.5 CenterZ=0 NormalX=0 NormalY=0 NormalZ=1 AngleXU=0 Radius=2.36714
    g18: LineSegment StartX=-29 StartY=-13.8671 StartZ=0 EndX=-26.95 EndY=-12.6836 EndZ=0
    g19: LineSegment StartX=-26.95 StartY=-12.6836 StartZ=0 EndX=-26.95 EndY=-10.3164 EndZ=0
    g20: LineSegment StartX=-26.95 StartY=-10.3164 StartZ=0 EndX=-29 EndY=-9.13286 EndZ=0
    g21: LineSegment StartX=-29 StartY=-9.13286 StartZ=0 EndX=-31.05 EndY=-10.3164 EndZ=0
    g22: LineSegment StartX=-31.05 StartY=-10.3164 StartZ=0 EndX=-31.05 EndY=-12.6836 EndZ=0
    g23: LineSegment StartX=-31.05 StartY=-12.6836 StartZ=0 EndX=-29 EndY=-13.8671 EndZ=0
    g24: Circle [constr] CenterX=-29 CenterY=-11.5 CenterZ=0 NormalX=0 NormalY=0 NormalZ=1 AngleXU=0 Radius=2.36714
    g25: LineSegment StartX=29 StartY=-13.8671 StartZ=0 EndX=31.05 EndY=-12.6836 EndZ=0
    g26: LineSegment StartX=31.05 StartY=-12.6836 StartZ=0 EndX=31.05 EndY=-10.3164 EndZ=0
    g27: LineSegment StartX=31.05 StartY=-10.3164 StartZ=0 EndX=29 EndY=-9.13286 EndZ=0
    g28: LineSegment StartX=29 StartY=-9.13286 StartZ=0 EndX=26.95 EndY=-10.3164 EndZ=0
    g29: LineSegment StartX=26.95 StartY=-10.3164 StartZ=0 EndX=26.95 EndY=-12.6836 EndZ=0
    g30: LineSegment StartX=26.95 StartY=-12.6836 StartZ=0 EndX=29 EndY=-13.8671 EndZ=0
    g31: Circle [constr] CenterX=29 CenterY=-11.5 CenterZ=0 NormalX=0 NormalY=0 NormalZ=1 AngleXU=0 Radius=2.36714
  constraints (72):
    c: Vertical(g0)
    c: Vertical(g1)
    c: Horizontal(g2)
    c: Horizontal(g3)
    c: PointOnObject(g-3,g3)
    c: PointOnObject(g-6,g2)
    c: PointOnObject(g-6,g1)
    c: PointOnObject(g-5,g0)
    c: Coincident(g4,g5)
    c: Coincident(g5,g6)
    c: Coincident(g6,g7)
    c: Coincident(g7,g8)
    c: Coincident(g8,g9)
    c: Coincident(g9,g4)
    c: Equal(g4, g5-g9) x5
    c: PointOnObject(g4,g10)
    c: PointOnObject(g5,g10)
    c: PointOnObject(g6,g10)
    c: PointOnObject(g7,g10)
    c: PointOnObject(g8,g10)
    c: PointOnObject(g9,g10)
    c: Coincident(g10,g-3)
    c: PointOnObject(g9,g1)
    c: DistanceX(g7,g5) = 4.1
    c: Coincident(g11,g12)
    c: Coincident(g12,g13)
    c: Coincident(g13,g14)
    c: Coincident(g14,g15)
    c: Coincident(g15,g16)
    c: Coincident(g16,g11)
    c: Equal(g11, g12-g16) x5
    c: PointOnObject(g11,g17)
    c: PointOnObject(g12,g17)
    c: PointOnObject(g13,g17)
    c: PointOnObject(g14,g17)
    c: PointOnObject(g15,g17)
    c: PointOnObject(g16,g17)
    c: Coincident(g17,g-4)
    c: PointOnObject(g16,g0)
    c: DistanceX(g14,g12) = 4.1
    c: Coincident(g18,g19)
    c: Coincident(g19,g20)
    c: Coincident(g20,g21)
    c: Coincident(g21,g22)
    c: Coincident(g22,g23)
    c: Coincident(g23,g18)
    c: Equal(g18, g19-g23) x5
    c: PointOnObject(g18,g24)
    c: PointOnObject(g19,g24)
    c: PointOnObject(g20,g24)
    c: PointOnObject(g21,g24)
    c: PointOnObject(g22,g24)
    c: PointOnObject(g23,g24)
    c: Coincident(g24,g-5)
    c: PointOnObject(g23,g0)
    c: DistanceX(g21,g19) = 4.1
    c: Coincident(g25,g26)
    c: Coincident(g26,g27)
    c: Coincident(g27,g28)
    c: Coincident(g28,g29)
    c: Coincident(g29,g30)
    c: Coincident(g30,g25)
    c: Equal(g25, g26-g30) x5
    c: PointOnObject(g25,g31)
    c: PointOnObject(g26,g31)
    c: PointOnObject(g27,g31)
    c: PointOnObject(g28,g31)
    c: PointOnObject(g29,g31)
    c: PointOnObject(g30,g31)
    c: Coincident(g31,g-6)
    c: PointOnObject(g30,g1)
    c: DistanceX(g28,g26) = 4.1
FEATURE [PartDesign::Pocket] Pocket005
  BaseFeature = -> Hole001
  Length = 2.5
  Length2 = 100
  Profile = -> Sketch010
  Type = 0
FEATURE [PartDesign::Fillet] Fillet
  Base = -> Pocket005 [Edge312,Edge306,Edge310,Edge308]
  BaseFeature = -> Pocket005
  Radius = 0.6
FEATURE [Sketcher::SketchObject] Sketch011
  ExternalGeometry = -> [Fillet]
  MapMode = 5
  Placement = pos=(32.8,0,0) rot=(0.57735,-0.57735,-0.57735;2.0944rad)
  Support = -> [Fillet]
  sketch-geometry (6):
    g0: LineSegment [constr] StartX=8.50001 StartY=4 StartZ=0 EndX=-8.09097 EndY=4 EndZ=0
    g1: LineSegment StartX=-9.5 StartY=8.5 StartZ=0 EndX=9.5 EndY=8.5 EndZ=0
    g2: LineSegment StartX=9.5 StartY=8.5 StartZ=0 EndX=9.5 EndY=5 EndZ=0
    g3: LineSegment StartX=9.5 StartY=5 StartZ=0 EndX=-9.5 EndY=5 EndZ=0
    g4: LineSegment StartX=-9.5 StartY=5 StartZ=0 EndX=-9.5 EndY=8.5 EndZ=0
    g5: LineSegment [constr] StartX=0 StartY=15.3767 StartZ=0 EndX=0 EndY=2.68391 EndZ=0
  constraints (16):
    c: Coincident(g0,g-3)
    c: Horizontal(g0)
    c: Coincident(g1,g2)
    c: Coincident(g2,g3)
    c: Coincident(g3,g4)
    c: Coincident(g4,g1)
    c: Horizontal(g1)
    c: Horizontal(g3)
    c: Vertical(g2)
    c: Vertical(g4)
    c: DistanceX(g1,g1) = 19
    c: PointOnObject(g5,g-2)
    c: Vertical(g5)
    c: Symmetric(g1,g1,g5)
    c: PointOnObject(g1,g-4)
    c: DistanceY(g0,g2) = 1
FEATURE [PartDesign::Pocket] Pocket006
  BaseFeature = -> Fillet
  Length = 0.7
  Length2 = 100
  Profile = -> Sketch011
  Type = 0
FEATURE [Sketcher::SketchObject] Sketch012
  ExternalGeometry = -> [Pocket006]
  MapMode = 5
  Placement = pos=(-32.8,0,0) rot=(0.57735,0.57735,0.57735;2.0944rad)
  Support = -> [Pocket006]
  sketch-geometry (15):
    g0: LineSegment [constr] StartX=8.97421 StartY=8.5 StartZ=0 EndX=8.97421 EndY=4.11024 EndZ=0
    g1: LineSegment [constr] StartX=-5.62579 StartY=8.5 StartZ=0 EndX=-5.62579 EndY=3.6342 EndZ=0
    g2: LineSegment [constr] StartX=-5.62579 StartY=8.5 StartZ=0 EndX=8.97421 EndY=8.5 EndZ=0
    g3: LineSegment [constr] StartX=8.17421 StartY=9.09588 StartZ=0 EndX=8.17421 EndY=3.57816 EndZ=0
    g4: LineSegment [constr] StartX=-4.72579 StartY=9.58242 StartZ=0 EndX=-4.72579 EndY=4.4197 EndZ=0
    g5: LineSegment [constr] StartX=-8.15183 StartY=7.7 StartZ=0 EndX=11.8659 EndY=7.7 EndZ=0
    g6: LineSegment [constr] StartX=-6.90186 StartY=7.4 StartZ=0 EndX=10.8983 EndY=7.4 EndZ=0
    g7: LineSegment StartX=-5.62579 StartY=8.5 StartZ=0 EndX=-1.62579 EndY=8.5 EndZ=0
    g8: LineSegment StartX=-1.62579 StartY=8.5 StartZ=0 EndX=-1.62579 EndY=7.4 EndZ=0
    g9: LineSegment StartX=-1.62579 StartY=7.4 StartZ=0 EndX=-5.62579 EndY=7.4 EndZ=0
    g10: LineSegment StartX=-5.62579 StartY=7.4 StartZ=0 EndX=-5.62579 EndY=8.5 EndZ=0
    g11: LineSegment StartX=8.97421 StartY=8.5 StartZ=0 EndX=4.97421 EndY=8.5 EndZ=0
    g12: LineSegment StartX=4.97421 StartY=8.5 StartZ=0 EndX=4.97421 EndY=7.4 EndZ=0
    g13: LineSegment StartX=4.97421 StartY=7.4 StartZ=0 EndX=8.97421 EndY=7.4 EndZ=0
    g14: LineSegment StartX=8.97421 StartY=7.4 StartZ=0 EndX=8.97421 EndY=8.5 EndZ=0
  constraints (38):
    c: Vertical(g0)
    c: DistanceX(g-4,g0) = 1
    c: Vertical(g1)
    c: DistanceX(g1,g-5) = 1
    c: PointOnObject(g2,g-7)
    c: Horizontal(g2)
    c: Vertical(g3)
    c: DistanceX(g3,g0) = 0.8
    c: Vertical(g4)
    c: DistanceX(g1,g4) = 0.9
    c: Horizontal(g5)
    c: DistanceY(g5,g2) = 0.8
    c: Horizontal(g6)
    c: DistanceY(g6,g-7) = 1.1
    c: Coincident(g1,g2)
    c: Coincident(g2,g0)
    c: Coincident(g7,g8)
    c: Coincident(g8,g9)
    c: Coincident(g9,g10)
    c: Coincident(g10,g7)
    c: Horizontal(g7)
    c: Horizontal(g9)
    c: Vertical(g8)
    c: Vertical(g10)
    c: Coincident(g7,g1)
    c: PointOnObject(g8,g6)
    c: Coincident(g11,g12)
    c: Coincident(g12,g13)
    c: Coincident(g13,g14)
    c: Coincident(g14,g11)
    c: Horizontal(g11)
    c: Horizontal(g13)
    c: Vertical(g12)
    c: Vertical(g14)
    c: Coincident(g11,g0)
    c: PointOnObject(g12,g6)
    c: DistanceX(g7,g7) = 4
    c: DistanceX(g11,g11) = 4
FEATURE [PartDesign::Pad] Pad003
  BaseFeature = -> Pocket006
  Length = 4
  Length2 = 100
  Profile = -> Sketch012
  Type = 0
FEATURE [Sketcher::SketchObject] Sketch013
  AttachmentOffset = pos=(0,0,-1.5) rot=(0,0,1;0rad)
  ExternalGeometry = -> [Pad003]
  MapMode = 5
  Placement = pos=(-30.3,0,0) rot=(0.57735,0.57735,0.57735;2.0944rad)
  Support = -> [Pad003]
  sketch-geometry (21):
    g0: LineSegment StartX=8.97421 StartY=7.4 StartZ=0 EndX=4.97421 EndY=7.4 EndZ=0
    g1: LineSegment StartX=4.97421 StartY=7.4 StartZ=0 EndX=4.97421 EndY=7.4 EndZ=0
    g2-g7: Circle [constr] x6 (B-spline internal-alignment scaffolding for g8; pole/knot coordinates omitted)
    g8: BSplineCurve PolesCount=6 KnotsCount=4 Degree=3 IsPeriodic=0
    g9-g12: GeomPoint [constr] x4 (B-spline internal-alignment scaffolding for g8; pole/knot coordinates omitted)
    g13: LineSegment StartX=4.97421 StartY=7.65732 StartZ=0 EndX=4.97421 EndY=7.4 EndZ=0
    g14: LineSegment [constr] StartX=1.67421 StartY=9.90728 StartZ=0 EndX=1.67421 EndY=2.98327 EndZ=0
    g15: LineSegment [constr] StartX=7.97421 StartY=6.8 StartZ=0 EndX=7.97421 EndY=5 EndZ=0
    g16: LineSegment [constr] StartX=-4.62579 StartY=5 StartZ=0 EndX=7.97421 EndY=5 EndZ=0
    g17: LineSegment StartX=-4.62579 StartY=6.8 StartZ=0 EndX=-4.62579 EndY=6.7 EndZ=0
    g18: LineSegment StartX=-4.62579 StartY=6.7 StartZ=0 EndX=-1.62579 EndY=6.7 EndZ=0
    g19: BSplineCurve PolesCount=6 KnotsCount=4 Degree=3 IsPeriodic=0
    g20: LineSegment StartX=-1.62579 StartY=7.65732 StartZ=0 EndX=-1.62579 EndY=6.7 EndZ=0
  constraints (22):
    c: Coincident(g-4,g0)
    c: Coincident(g0,g-4)
    c: Coincident(g0,g1)
    c: Coincident(g1,g-5)
    c: Coincident(g8,g0)
    c: Radius(g2) = 0.02
    c: Equal(g2, g3-g7) x5
    c: PointOnObject(g8,g-5)
    c: InternalAlignment(g2-g7 -> g8) x6
    c: InternalAlignment(g9-g12 -> g8) x4
    c: Coincident(g13,g8)
    c: Coincident(g13,g1)
    c: Vertical(g14)
    c: Coincident(g15,g-6)
    c: PointOnObject(g15,g-6)
    c: PointOnObject(g16,g-7)
    c: Coincident(g16,g-7)
    c: Symmetric(g15,g16,g14)
    c: Coincident(g17,g18)
    c: Coincident(g19,g17)
    c: Coincident(g20,g19)
    c: Coincident(g20,g18)
FEATURE [PartDesign::Pocket] Pocket007
  BaseFeature = -> Pad003
  Length = 2.5
  Length2 = 100
  Profile = -> Sketch013
  Type = 0
FEATURE [PartDesign::Fillet] Fillet001
  Base = -> Pocket007 [Edge443,Edge447]
  BaseFeature = -> Pocket007
  Radius = 0.2
FEATURE [PartDesign::Fillet] Fillet002
  Base = -> Fillet001 [Edge42,Edge19,Edge147,Edge105]
  BaseFeature = -> Fillet001
  Radius = 1
FEATURE [PartDesign::Fillet] Fillet003
  Base = -> Fillet002 [Edge26,Edge52,Edge15,Edge41]
  BaseFeature = -> Fillet002
  Radius = 2
FEATURE [PartDesign::Fillet] Fillet004
  Base = -> Fillet003 [Edge41,Edge182,Edge176,Edge88]
  BaseFeature = -> Fillet003
  Radius = 0.1
FEATURE [PartDesign::Body] Body
  Group = -> [Sketch,Sketch001,Pad,Sketch002,Pocket,Sketch003,Pad001,Sketch004,Pad002,Sketch005,Pocket002,Sketch006,Pocket003,Chamfer,Sketch007,Hole,Sketch008,Pocket004,Sketch009,Hole001,Sketch010,Pocket005,Fillet,Sketch011,Pocket006,Sketch012,Pad003,Sketch013,Pocket007,Fillet001,Fillet002,Fillet003,Fillet004]
  Origin = -> Origin
  Tip = -> Fillet004
FEATURE [Mesh::Feature] Mesh  label="Fillet004 (Meshed)"
